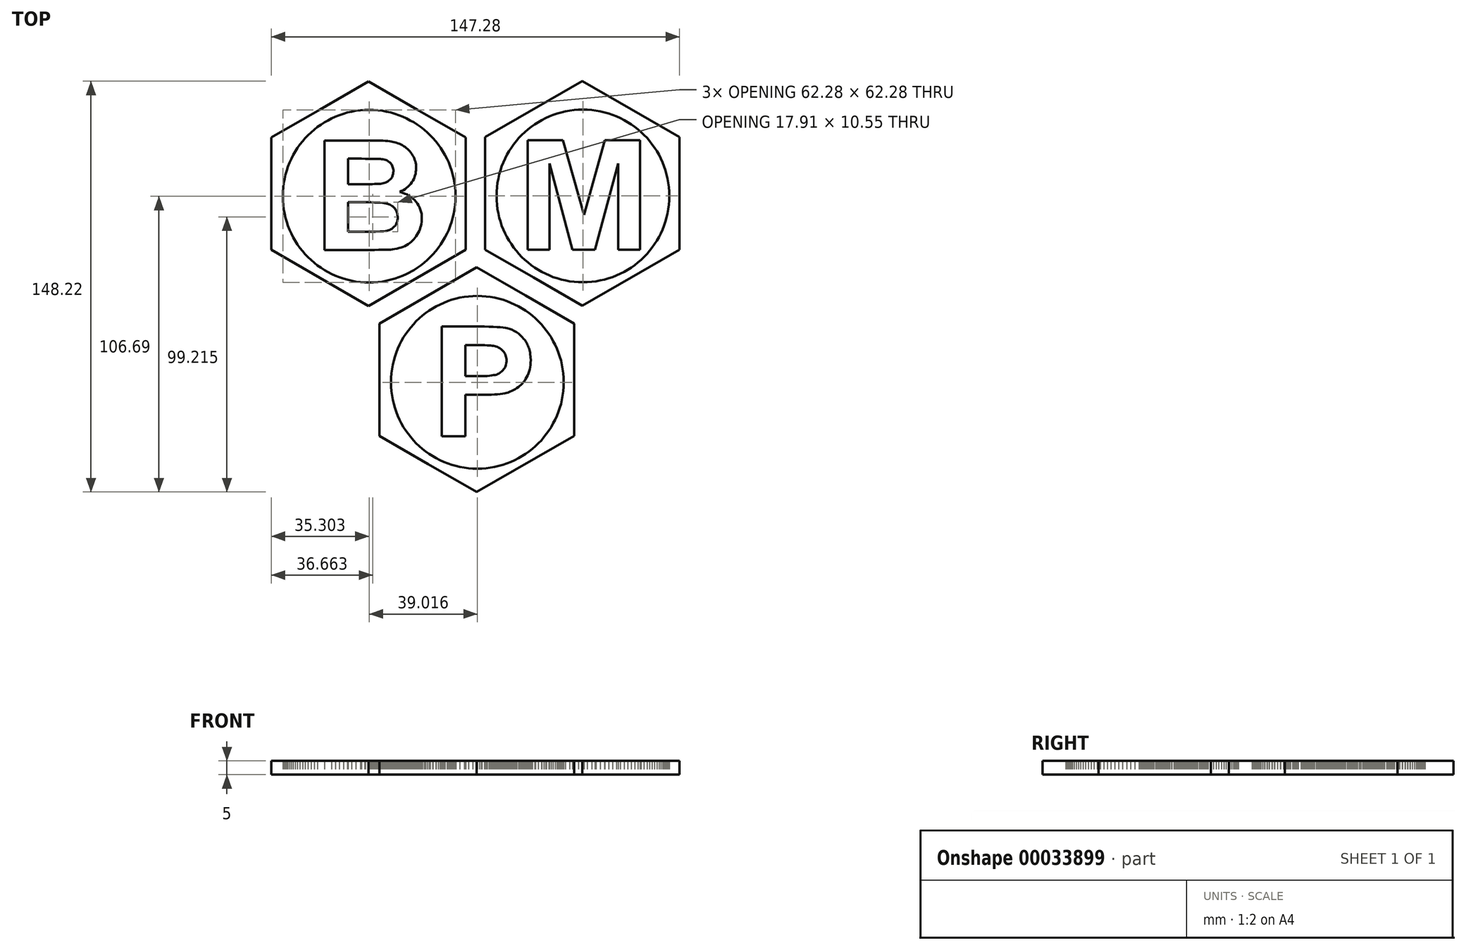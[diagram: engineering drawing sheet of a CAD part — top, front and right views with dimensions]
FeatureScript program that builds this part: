
annotation { "Feature Type Name" : "Feature", "Feature Type Description" : "" }
export const myFeature = defineFeature(function(context is Context, id is Id, definition is map)
    precondition{}
    {
        {
            var Q0;
            Q0=qCreatedBy(makeId("Top.planeOp"),FACE);
            var sketch = newSketch(context, id + "F0", { "sketchPlane" : qUnion([Q0])});
            skLineSegment(sketch, "E0", {"start": v(38.58, 74.11) * mm, "end": v(56.13, 64) * mm});
            skLineSegment(sketch, "E1", {"start": v(56.13, 64) * mm, "end": v(73.64, 53.89) * mm});
            skLineSegment(sketch, "E2", {"start": v(73.64, 53.89) * mm, "end": v(73.64, 33.62) * mm});
            skLineSegment(sketch, "E3", {"start": v(73.64, 33.62) * mm, "end": v(73.64, 13.35) * mm});
            skLineSegment(sketch, "E4", {"start": v(73.64, 13.35) * mm, "end": v(56.13, 3.24) * mm});
            skLineSegment(sketch, "E5", {"start": v(56.13, 3.24) * mm, "end": v(38.58, -6.92) * mm});
            skLineSegment(sketch, "E6", {"start": v(38.58, -6.92) * mm, "end": v(21.03, 3.24) * mm});
            skLineSegment(sketch, "E7", {"start": v(21.03, 3.24) * mm, "end": v(3.48, 13.35) * mm});
            skLineSegment(sketch, "E8", {"start": v(3.48, 13.35) * mm, "end": v(3.48, 33.62) * mm});
            skLineSegment(sketch, "E9", {"start": v(3.48, 33.62) * mm, "end": v(3.48, 53.89) * mm});
            skLineSegment(sketch, "E10", {"start": v(3.48, 53.89) * mm, "end": v(21.03, 64) * mm});
            skLineSegment(sketch, "E11", {"start": v(21.03, 64) * mm, "end": v(38.58, 74.11) * mm});
            skLineSegment(sketch, "E12", {"start": v(38.78, 63.84) * mm, "end": v(40.38, 63.8) * mm});
            skLineSegment(sketch, "E13", {"start": v(40.38, 63.8) * mm, "end": v(41.97, 63.68) * mm});
            skLineSegment(sketch, "E14", {"start": v(41.97, 63.68) * mm, "end": v(43.53, 63.48) * mm});
            skLineSegment(sketch, "E15", {"start": v(43.53, 63.48) * mm, "end": v(45.05, 63.2) * mm});
            skLineSegment(sketch, "E16", {"start": v(45.05, 63.2) * mm, "end": v(46.57, 62.84) * mm});
            skLineSegment(sketch, "E17", {"start": v(46.57, 62.84) * mm, "end": v(48.05, 62.44) * mm});
            skLineSegment(sketch, "E18", {"start": v(48.05, 62.44) * mm, "end": v(49.49, 61.96) * mm});
            skLineSegment(sketch, "E19", {"start": v(49.49, 61.96) * mm, "end": v(50.89, 61.4) * mm});
            skLineSegment(sketch, "E20", {"start": v(50.89, 61.4) * mm, "end": v(52.29, 60.76) * mm});
            skLineSegment(sketch, "E21", {"start": v(52.29, 60.76) * mm, "end": v(53.6, 60.08) * mm});
            skLineSegment(sketch, "E22", {"start": v(53.6, 60.08) * mm, "end": v(54.93, 59.32) * mm});
            skLineSegment(sketch, "E23", {"start": v(54.93, 59.32) * mm, "end": v(56.17, 58.52) * mm});
            skLineSegment(sketch, "E24", {"start": v(56.17, 58.52) * mm, "end": v(57.4, 57.64) * mm});
            skLineSegment(sketch, "E25", {"start": v(57.4, 57.64) * mm, "end": v(58.56, 56.73) * mm});
            skLineSegment(sketch, "E26", {"start": v(58.56, 56.73) * mm, "end": v(59.72, 55.77) * mm});
            skLineSegment(sketch, "E27", {"start": v(59.72, 55.77) * mm, "end": v(60.8, 54.73) * mm});
            skLineSegment(sketch, "E28", {"start": v(60.8, 54.73) * mm, "end": v(61.84, 53.65) * mm});
            skLineSegment(sketch, "E29", {"start": v(61.84, 53.65) * mm, "end": v(62.8, 52.49) * mm});
            skLineSegment(sketch, "E30", {"start": v(62.8, 52.49) * mm, "end": v(63.72, 51.33) * mm});
            skLineSegment(sketch, "E31", {"start": v(63.72, 51.33) * mm, "end": v(64.6, 50.09) * mm});
            skLineSegment(sketch, "E32", {"start": v(64.6, 50.09) * mm, "end": v(65.4, 48.85) * mm});
            skLineSegment(sketch, "E33", {"start": v(65.4, 48.85) * mm, "end": v(66.16, 47.53) * mm});
            skLineSegment(sketch, "E34", {"start": v(66.16, 47.53) * mm, "end": v(66.84, 46.21) * mm});
            skLineSegment(sketch, "E35", {"start": v(66.84, 46.21) * mm, "end": v(67.48, 44.81) * mm});
            skLineSegment(sketch, "E36", {"start": v(67.48, 44.81) * mm, "end": v(68.04, 43.41) * mm});
            skLineSegment(sketch, "E37", {"start": v(68.04, 43.41) * mm, "end": v(68.52, 41.97) * mm});
            skLineSegment(sketch, "E38", {"start": v(68.52, 41.97) * mm, "end": v(68.92, 40.5) * mm});
            skLineSegment(sketch, "E39", {"start": v(68.92, 40.5) * mm, "end": v(69.28, 38.98) * mm});
            skLineSegment(sketch, "E40", {"start": v(69.28, 38.98) * mm, "end": v(69.56, 37.46) * mm});
            skLineSegment(sketch, "E41", {"start": v(69.56, 37.46) * mm, "end": v(69.76, 35.9) * mm});
            skLineSegment(sketch, "E42", {"start": v(69.76, 35.9) * mm, "end": v(69.88, 34.3) * mm});
            skLineSegment(sketch, "E43", {"start": v(69.88, 34.3) * mm, "end": v(69.92, 32.7) * mm});
            skLineSegment(sketch, "E44", {"start": v(69.92, 32.7) * mm, "end": v(69.88, 31.1) * mm});
            skLineSegment(sketch, "E45", {"start": v(69.88, 31.1) * mm, "end": v(69.76, 29.5) * mm});
            skLineSegment(sketch, "E46", {"start": v(69.76, 29.5) * mm, "end": v(69.56, 27.94) * mm});
            skLineSegment(sketch, "E47", {"start": v(69.56, 27.94) * mm, "end": v(69.28, 26.42) * mm});
            skLineSegment(sketch, "E48", {"start": v(69.28, 26.42) * mm, "end": v(68.92, 24.9) * mm});
            skLineSegment(sketch, "E49", {"start": v(68.92, 24.9) * mm, "end": v(68.52, 23.43) * mm});
            skLineSegment(sketch, "E50", {"start": v(68.52, 23.43) * mm, "end": v(68.04, 21.99) * mm});
            skLineSegment(sketch, "E51", {"start": v(68.04, 21.99) * mm, "end": v(67.48, 20.59) * mm});
            skLineSegment(sketch, "E52", {"start": v(67.48, 20.59) * mm, "end": v(66.84, 19.19) * mm});
            skLineSegment(sketch, "E53", {"start": v(66.84, 19.19) * mm, "end": v(66.16, 17.87) * mm});
            skLineSegment(sketch, "E54", {"start": v(66.16, 17.87) * mm, "end": v(65.4, 16.55) * mm});
            skLineSegment(sketch, "E55", {"start": v(65.4, 16.55) * mm, "end": v(64.6, 15.27) * mm});
            skLineSegment(sketch, "E56", {"start": v(64.6, 15.27) * mm, "end": v(63.72, 14.07) * mm});
            skLineSegment(sketch, "E57", {"start": v(63.72, 14.07) * mm, "end": v(62.8, 12.87) * mm});
            skLineSegment(sketch, "E58", {"start": v(62.8, 12.87) * mm, "end": v(61.84, 11.75) * mm});
            skLineSegment(sketch, "E59", {"start": v(61.84, 11.75) * mm, "end": v(60.8, 10.67) * mm});
            skLineSegment(sketch, "E60", {"start": v(60.8, 10.67) * mm, "end": v(59.72, 9.63) * mm});
            skLineSegment(sketch, "E61", {"start": v(59.72, 9.63) * mm, "end": v(58.56, 8.67) * mm});
            skLineSegment(sketch, "E62", {"start": v(58.56, 8.67) * mm, "end": v(57.4, 7.76) * mm});
            skLineSegment(sketch, "E63", {"start": v(57.4, 7.76) * mm, "end": v(56.17, 6.88) * mm});
            skLineSegment(sketch, "E64", {"start": v(56.17, 6.88) * mm, "end": v(54.93, 6.08) * mm});
            skLineSegment(sketch, "E65", {"start": v(54.93, 6.08) * mm, "end": v(53.6, 5.32) * mm});
            skLineSegment(sketch, "E66", {"start": v(53.6, 5.32) * mm, "end": v(52.29, 4.64) * mm});
            skLineSegment(sketch, "E67", {"start": v(52.29, 4.64) * mm, "end": v(50.89, 4) * mm});
            skLineSegment(sketch, "E68", {"start": v(50.89, 4) * mm, "end": v(49.49, 3.44) * mm});
            skLineSegment(sketch, "E69", {"start": v(49.49, 3.44) * mm, "end": v(48.05, 2.96) * mm});
            skLineSegment(sketch, "E70", {"start": v(48.05, 2.96) * mm, "end": v(46.57, 2.52) * mm});
            skLineSegment(sketch, "E71", {"start": v(46.57, 2.52) * mm, "end": v(45.05, 2.2) * mm});
            skLineSegment(sketch, "E72", {"start": v(45.05, 2.2) * mm, "end": v(43.53, 1.92) * mm});
            skLineSegment(sketch, "E73", {"start": v(43.53, 1.92) * mm, "end": v(41.97, 1.72) * mm});
            skLineSegment(sketch, "E74", {"start": v(41.97, 1.72) * mm, "end": v(40.38, 1.6) * mm});
            skLineSegment(sketch, "E75", {"start": v(40.38, 1.6) * mm, "end": v(38.78, 1.56) * mm});
            skLineSegment(sketch, "E76", {"start": v(38.78, 1.56) * mm, "end": v(37.18, 1.6) * mm});
            skLineSegment(sketch, "E77", {"start": v(37.18, 1.6) * mm, "end": v(35.58, 1.72) * mm});
            skLineSegment(sketch, "E78", {"start": v(35.58, 1.72) * mm, "end": v(34.02, 1.92) * mm});
            skLineSegment(sketch, "E79", {"start": v(34.02, 1.92) * mm, "end": v(32.5, 2.2) * mm});
            skLineSegment(sketch, "E80", {"start": v(32.5, 2.2) * mm, "end": v(30.98, 2.52) * mm});
            skLineSegment(sketch, "E81", {"start": v(30.98, 2.52) * mm, "end": v(29.5, 2.96) * mm});
            skLineSegment(sketch, "E82", {"start": v(29.5, 2.96) * mm, "end": v(28.06, 3.44) * mm});
            skLineSegment(sketch, "E83", {"start": v(28.06, 3.44) * mm, "end": v(26.66, 4) * mm});
            skLineSegment(sketch, "E84", {"start": v(26.66, 4) * mm, "end": v(25.26, 4.64) * mm});
            skLineSegment(sketch, "E85", {"start": v(25.26, 4.64) * mm, "end": v(23.95, 5.32) * mm});
            skLineSegment(sketch, "E86", {"start": v(23.95, 5.32) * mm, "end": v(22.63, 6.08) * mm});
            skLineSegment(sketch, "E87", {"start": v(22.63, 6.08) * mm, "end": v(21.35, 6.88) * mm});
            skLineSegment(sketch, "E88", {"start": v(21.35, 6.88) * mm, "end": v(20.15, 7.76) * mm});
            skLineSegment(sketch, "E89", {"start": v(20.15, 7.76) * mm, "end": v(18.95, 8.67) * mm});
            skLineSegment(sketch, "E90", {"start": v(18.95, 8.67) * mm, "end": v(17.83, 9.63) * mm});
            skLineSegment(sketch, "E91", {"start": v(17.83, 9.63) * mm, "end": v(16.75, 10.67) * mm});
            skLineSegment(sketch, "E92", {"start": v(16.75, 10.67) * mm, "end": v(15.71, 11.75) * mm});
            skLineSegment(sketch, "E93", {"start": v(15.71, 11.75) * mm, "end": v(14.75, 12.87) * mm});
            skLineSegment(sketch, "E94", {"start": v(14.75, 12.87) * mm, "end": v(13.83, 14.07) * mm});
            skLineSegment(sketch, "E95", {"start": v(13.83, 14.07) * mm, "end": v(12.95, 15.27) * mm});
            skLineSegment(sketch, "E96", {"start": v(12.95, 15.27) * mm, "end": v(12.15, 16.55) * mm});
            skLineSegment(sketch, "E97", {"start": v(12.15, 16.55) * mm, "end": v(11.4, 17.87) * mm});
            skLineSegment(sketch, "E98", {"start": v(11.4, 17.87) * mm, "end": v(10.71, 19.19) * mm});
            skLineSegment(sketch, "E99", {"start": v(10.71, 19.19) * mm, "end": v(10.07, 20.59) * mm});
            skLineSegment(sketch, "E100", {"start": v(10.07, 20.59) * mm, "end": v(9.51, 21.99) * mm});
            skLineSegment(sketch, "E101", {"start": v(9.51, 21.99) * mm, "end": v(9.03, 23.43) * mm});
            skLineSegment(sketch, "E102", {"start": v(9.03, 23.43) * mm, "end": v(8.6, 24.9) * mm});
            skLineSegment(sketch, "E103", {"start": v(8.6, 24.9) * mm, "end": v(8.27, 26.42) * mm});
            skLineSegment(sketch, "E104", {"start": v(8.27, 26.42) * mm, "end": v(8, 27.94) * mm});
            skLineSegment(sketch, "E105", {"start": v(8, 27.94) * mm, "end": v(7.8, 29.5) * mm});
            skLineSegment(sketch, "E106", {"start": v(7.8, 29.5) * mm, "end": v(7.68, 31.1) * mm});
            skLineSegment(sketch, "E107", {"start": v(7.68, 31.1) * mm, "end": v(7.64, 32.7) * mm});
            skLineSegment(sketch, "E108", {"start": v(7.64, 32.7) * mm, "end": v(7.68, 34.3) * mm});
            skLineSegment(sketch, "E109", {"start": v(7.68, 34.3) * mm, "end": v(7.8, 35.9) * mm});
            skLineSegment(sketch, "E110", {"start": v(7.8, 35.9) * mm, "end": v(8, 37.46) * mm});
            skLineSegment(sketch, "E111", {"start": v(8, 37.46) * mm, "end": v(8.27, 38.98) * mm});
            skLineSegment(sketch, "E112", {"start": v(8.27, 38.98) * mm, "end": v(8.6, 40.5) * mm});
            skLineSegment(sketch, "E113", {"start": v(8.6, 40.5) * mm, "end": v(9.03, 41.97) * mm});
            skLineSegment(sketch, "E114", {"start": v(9.03, 41.97) * mm, "end": v(9.51, 43.41) * mm});
            skLineSegment(sketch, "E115", {"start": v(9.51, 43.41) * mm, "end": v(10.07, 44.81) * mm});
            skLineSegment(sketch, "E116", {"start": v(10.07, 44.81) * mm, "end": v(10.71, 46.21) * mm});
            skLineSegment(sketch, "E117", {"start": v(10.71, 46.21) * mm, "end": v(11.4, 47.53) * mm});
            skLineSegment(sketch, "E118", {"start": v(11.4, 47.53) * mm, "end": v(12.15, 48.85) * mm});
            skLineSegment(sketch, "E119", {"start": v(12.15, 48.85) * mm, "end": v(12.95, 50.09) * mm});
            skLineSegment(sketch, "E120", {"start": v(12.95, 50.09) * mm, "end": v(13.83, 51.33) * mm});
            skLineSegment(sketch, "E121", {"start": v(13.83, 51.33) * mm, "end": v(14.75, 52.49) * mm});
            skLineSegment(sketch, "E122", {"start": v(14.75, 52.49) * mm, "end": v(15.71, 53.65) * mm});
            skLineSegment(sketch, "E123", {"start": v(15.71, 53.65) * mm, "end": v(16.75, 54.73) * mm});
            skLineSegment(sketch, "E124", {"start": v(16.75, 54.73) * mm, "end": v(17.83, 55.77) * mm});
            skLineSegment(sketch, "E125", {"start": v(17.83, 55.77) * mm, "end": v(18.95, 56.73) * mm});
            skLineSegment(sketch, "E126", {"start": v(18.95, 56.73) * mm, "end": v(20.15, 57.64) * mm});
            skLineSegment(sketch, "E127", {"start": v(20.15, 57.64) * mm, "end": v(21.35, 58.52) * mm});
            skLineSegment(sketch, "E128", {"start": v(21.35, 58.52) * mm, "end": v(22.63, 59.32) * mm});
            skLineSegment(sketch, "E129", {"start": v(22.63, 59.32) * mm, "end": v(23.95, 60.08) * mm});
            skLineSegment(sketch, "E130", {"start": v(23.95, 60.08) * mm, "end": v(25.26, 60.76) * mm});
            skLineSegment(sketch, "E131", {"start": v(25.26, 60.76) * mm, "end": v(26.66, 61.4) * mm});
            skLineSegment(sketch, "E132", {"start": v(26.66, 61.4) * mm, "end": v(28.06, 61.96) * mm});
            skLineSegment(sketch, "E133", {"start": v(28.06, 61.96) * mm, "end": v(29.5, 62.44) * mm});
            skLineSegment(sketch, "E134", {"start": v(29.5, 62.44) * mm, "end": v(30.98, 62.84) * mm});
            skLineSegment(sketch, "E135", {"start": v(30.98, 62.84) * mm, "end": v(32.5, 63.2) * mm});
            skLineSegment(sketch, "E136", {"start": v(32.5, 63.2) * mm, "end": v(34.02, 63.48) * mm});
            skLineSegment(sketch, "E137", {"start": v(34.02, 63.48) * mm, "end": v(35.58, 63.68) * mm});
            skLineSegment(sketch, "E138", {"start": v(35.58, 63.68) * mm, "end": v(37.18, 63.8) * mm});
            skLineSegment(sketch, "E139", {"start": v(37.18, 63.8) * mm, "end": v(38.78, 63.84) * mm});
            skLineSegment(sketch, "E140", {"start": v(18.87, 13.23) * mm, "end": v(18.87, 52.8) * mm});
            skLineSegment(sketch, "E141", {"start": v(18.87, 52.8) * mm, "end": v(31.54, 52.8) * mm});
            skLineSegment(sketch, "E142", {"start": v(31.54, 52.8) * mm, "end": v(39.14, 25.82) * mm});
            skLineSegment(sketch, "E143", {"start": v(39.14, 25.82) * mm, "end": v(46.61, 52.8) * mm});
            skLineSegment(sketch, "E144", {"start": v(46.61, 52.8) * mm, "end": v(59.32, 52.8) * mm});
            skLineSegment(sketch, "E145", {"start": v(59.32, 52.8) * mm, "end": v(59.32, 13.23) * mm});
            skLineSegment(sketch, "E146", {"start": v(59.32, 13.23) * mm, "end": v(51.45, 13.23) * mm});
            skLineSegment(sketch, "E147", {"start": v(51.45, 13.23) * mm, "end": v(51.45, 44.37) * mm});
            skLineSegment(sketch, "E148", {"start": v(51.45, 44.37) * mm, "end": v(43.13, 13.23) * mm});
            skLineSegment(sketch, "E149", {"start": v(43.13, 13.23) * mm, "end": v(35.02, 13.23) * mm});
            skLineSegment(sketch, "E150", {"start": v(35.02, 13.23) * mm, "end": v(26.7, 44.37) * mm});
            skLineSegment(sketch, "E151", {"start": v(26.7, 44.37) * mm, "end": v(26.7, 13.23) * mm});
            skLineSegment(sketch, "E152", {"start": v(26.7, 13.23) * mm, "end": v(18.87, 13.23) * mm});
            skLineSegment(sketch, "E153", {"start": v(-38.54, 74.03) * mm, "end": v(-20.99, 63.88) * mm});
            skLineSegment(sketch, "E154", {"start": v(-20.99, 63.88) * mm, "end": v(-3.44, 53.77) * mm});
            skLineSegment(sketch, "E155", {"start": v(-3.44, 53.77) * mm, "end": v(-3.44, 33.5) * mm});
            skLineSegment(sketch, "E156", {"start": v(-3.44, 33.5) * mm, "end": v(-3.44, 13.27) * mm});
            skLineSegment(sketch, "E157", {"start": v(-3.44, 13.27) * mm, "end": v(-20.99, 3.12) * mm});
            skLineSegment(sketch, "E158", {"start": v(-20.99, 3.12) * mm, "end": v(-38.54, -7) * mm});
            skLineSegment(sketch, "E159", {"start": v(-38.54, -7) * mm, "end": v(-56.09, 3.12) * mm});
            skLineSegment(sketch, "E160", {"start": v(-56.09, 3.12) * mm, "end": v(-73.64, 13.27) * mm});
            skLineSegment(sketch, "E161", {"start": v(-73.64, 13.27) * mm, "end": v(-73.64, 33.5) * mm});
            skLineSegment(sketch, "E162", {"start": v(-73.64, 33.5) * mm, "end": v(-73.64, 53.77) * mm});
            skLineSegment(sketch, "E163", {"start": v(-73.64, 53.77) * mm, "end": v(-56.09, 63.88) * mm});
            skLineSegment(sketch, "E164", {"start": v(-56.09, 63.88) * mm, "end": v(-38.54, 74.03) * mm});
            skLineSegment(sketch, "E165", {"start": v(-38.34, 63.72) * mm, "end": v(-36.74, 63.68) * mm});
            skLineSegment(sketch, "E166", {"start": v(-36.74, 63.68) * mm, "end": v(-35.14, 63.56) * mm});
            skLineSegment(sketch, "E167", {"start": v(-35.14, 63.56) * mm, "end": v(-33.58, 63.4) * mm});
            skLineSegment(sketch, "E168", {"start": v(-33.58, 63.4) * mm, "end": v(-32.06, 63.12) * mm});
            skLineSegment(sketch, "E169", {"start": v(-32.06, 63.12) * mm, "end": v(-30.54, 62.76) * mm});
            skLineSegment(sketch, "E170", {"start": v(-30.54, 62.76) * mm, "end": v(-29.06, 62.32) * mm});
            skLineSegment(sketch, "E171", {"start": v(-29.06, 62.32) * mm, "end": v(-27.62, 61.84) * mm});
            skLineSegment(sketch, "E172", {"start": v(-27.62, 61.84) * mm, "end": v(-26.22, 61.28) * mm});
            skLineSegment(sketch, "E173", {"start": v(-26.22, 61.28) * mm, "end": v(-24.82, 60.68) * mm});
            skLineSegment(sketch, "E174", {"start": v(-24.82, 60.68) * mm, "end": v(-23.5, 59.96) * mm});
            skLineSegment(sketch, "E175", {"start": v(-23.5, 59.96) * mm, "end": v(-22.19, 59.24) * mm});
            skLineSegment(sketch, "E176", {"start": v(-22.19, 59.24) * mm, "end": v(-20.9, 58.4) * mm});
            skLineSegment(sketch, "E177", {"start": v(-20.9, 58.4) * mm, "end": v(-19.7, 57.56) * mm});
            skLineSegment(sketch, "E178", {"start": v(-19.7, 57.56) * mm, "end": v(-18.5, 56.65) * mm});
            skLineSegment(sketch, "E179", {"start": v(-18.5, 56.65) * mm, "end": v(-17.39, 55.65) * mm});
            skLineSegment(sketch, "E180", {"start": v(-17.39, 55.65) * mm, "end": v(-16.31, 54.6) * mm});
            skLineSegment(sketch, "E181", {"start": v(-16.31, 54.6) * mm, "end": v(-15.27, 53.53) * mm});
            skLineSegment(sketch, "E182", {"start": v(-15.27, 53.53) * mm, "end": v(-14.31, 52.4) * mm});
            skLineSegment(sketch, "E183", {"start": v(-14.31, 52.4) * mm, "end": v(-13.4, 51.25) * mm});
            skLineSegment(sketch, "E184", {"start": v(-13.4, 51.25) * mm, "end": v(-12.51, 50) * mm});
            skLineSegment(sketch, "E185", {"start": v(-12.51, 50) * mm, "end": v(-11.71, 48.73) * mm});
            skLineSegment(sketch, "E186", {"start": v(-11.71, 48.73) * mm, "end": v(-10.95, 47.45) * mm});
            skLineSegment(sketch, "E187", {"start": v(-10.95, 47.45) * mm, "end": v(-10.27, 46.1) * mm});
            skLineSegment(sketch, "E188", {"start": v(-10.27, 46.1) * mm, "end": v(-9.63, 44.73) * mm});
            skLineSegment(sketch, "E189", {"start": v(-9.63, 44.73) * mm, "end": v(-9.07, 43.3) * mm});
            skLineSegment(sketch, "E190", {"start": v(-9.07, 43.3) * mm, "end": v(-8.6, 41.85) * mm});
            skLineSegment(sketch, "E191", {"start": v(-8.6, 41.85) * mm, "end": v(-8.16, 40.38) * mm});
            skLineSegment(sketch, "E192", {"start": v(-8.16, 40.38) * mm, "end": v(-7.84, 38.86) * mm});
            skLineSegment(sketch, "E193", {"start": v(-7.84, 38.86) * mm, "end": v(-7.56, 37.34) * mm});
            skLineSegment(sketch, "E194", {"start": v(-7.56, 37.34) * mm, "end": v(-7.36, 35.78) * mm});
            skLineSegment(sketch, "E195", {"start": v(-7.36, 35.78) * mm, "end": v(-7.24, 34.22) * mm});
            skLineSegment(sketch, "E196", {"start": v(-7.24, 34.22) * mm, "end": v(-7.2, 32.58) * mm});
            skLineSegment(sketch, "E197", {"start": v(-7.2, 32.58) * mm, "end": v(-7.24, 30.98) * mm});
            skLineSegment(sketch, "E198", {"start": v(-7.24, 30.98) * mm, "end": v(-7.36, 29.42) * mm});
            skLineSegment(sketch, "E199", {"start": v(-7.36, 29.42) * mm, "end": v(-7.56, 27.86) * mm});
            skLineSegment(sketch, "E200", {"start": v(-7.56, 27.86) * mm, "end": v(-7.84, 26.3) * mm});
            skLineSegment(sketch, "E201", {"start": v(-7.84, 26.3) * mm, "end": v(-8.16, 24.82) * mm});
            skLineSegment(sketch, "E202", {"start": v(-8.16, 24.82) * mm, "end": v(-8.6, 23.35) * mm});
            skLineSegment(sketch, "E203", {"start": v(-8.6, 23.35) * mm, "end": v(-9.07, 21.9) * mm});
            skLineSegment(sketch, "E204", {"start": v(-9.07, 21.9) * mm, "end": v(-9.63, 20.47) * mm});
            skLineSegment(sketch, "E205", {"start": v(-9.63, 20.47) * mm, "end": v(-10.27, 19.1) * mm});
            skLineSegment(sketch, "E206", {"start": v(-10.27, 19.1) * mm, "end": v(-10.95, 17.75) * mm});
            skLineSegment(sketch, "E207", {"start": v(-10.95, 17.75) * mm, "end": v(-11.71, 16.47) * mm});
            skLineSegment(sketch, "E208", {"start": v(-11.71, 16.47) * mm, "end": v(-12.51, 15.2) * mm});
            skLineSegment(sketch, "E209", {"start": v(-12.51, 15.2) * mm, "end": v(-13.4, 13.95) * mm});
            skLineSegment(sketch, "E210", {"start": v(-13.4, 13.95) * mm, "end": v(-14.31, 12.8) * mm});
            skLineSegment(sketch, "E211", {"start": v(-14.31, 12.8) * mm, "end": v(-15.27, 11.67) * mm});
            skLineSegment(sketch, "E212", {"start": v(-15.27, 11.67) * mm, "end": v(-16.31, 10.6) * mm});
            skLineSegment(sketch, "E213", {"start": v(-16.31, 10.6) * mm, "end": v(-17.39, 9.55) * mm});
            skLineSegment(sketch, "E214", {"start": v(-17.39, 9.55) * mm, "end": v(-18.5, 8.55) * mm});
            skLineSegment(sketch, "E215", {"start": v(-18.5, 8.55) * mm, "end": v(-19.7, 7.64) * mm});
            skLineSegment(sketch, "E216", {"start": v(-19.7, 7.64) * mm, "end": v(-20.9, 6.8) * mm});
            skLineSegment(sketch, "E217", {"start": v(-20.9, 6.8) * mm, "end": v(-22.19, 5.96) * mm});
            skLineSegment(sketch, "E218", {"start": v(-22.19, 5.96) * mm, "end": v(-23.5, 5.24) * mm});
            skLineSegment(sketch, "E219", {"start": v(-23.5, 5.24) * mm, "end": v(-24.82, 4.52) * mm});
            skLineSegment(sketch, "E220", {"start": v(-24.82, 4.52) * mm, "end": v(-26.22, 3.92) * mm});
            skLineSegment(sketch, "E221", {"start": v(-26.22, 3.92) * mm, "end": v(-27.62, 3.36) * mm});
            skLineSegment(sketch, "E222", {"start": v(-27.62, 3.36) * mm, "end": v(-29.06, 2.84) * mm});
            skLineSegment(sketch, "E223", {"start": v(-29.06, 2.84) * mm, "end": v(-30.54, 2.44) * mm});
            skLineSegment(sketch, "E224", {"start": v(-30.54, 2.44) * mm, "end": v(-32.06, 2.08) * mm});
            skLineSegment(sketch, "E225", {"start": v(-32.06, 2.08) * mm, "end": v(-33.58, 1.8) * mm});
            skLineSegment(sketch, "E226", {"start": v(-33.58, 1.8) * mm, "end": v(-35.14, 1.6) * mm});
            skLineSegment(sketch, "E227", {"start": v(-35.14, 1.6) * mm, "end": v(-36.74, 1.48) * mm});
            skLineSegment(sketch, "E228", {"start": v(-36.74, 1.48) * mm, "end": v(-38.34, 1.44) * mm});
            skLineSegment(sketch, "E229", {"start": v(-38.34, 1.44) * mm, "end": v(-39.94, 1.48) * mm});
            skLineSegment(sketch, "E230", {"start": v(-39.94, 1.48) * mm, "end": v(-41.53, 1.6) * mm});
            skLineSegment(sketch, "E231", {"start": v(-41.53, 1.6) * mm, "end": v(-43.1, 1.8) * mm});
            skLineSegment(sketch, "E232", {"start": v(-43.1, 1.8) * mm, "end": v(-44.61, 2.08) * mm});
            skLineSegment(sketch, "E233", {"start": v(-44.61, 2.08) * mm, "end": v(-46.13, 2.44) * mm});
            skLineSegment(sketch, "E234", {"start": v(-46.13, 2.44) * mm, "end": v(-47.61, 2.84) * mm});
            skLineSegment(sketch, "E235", {"start": v(-47.61, 2.84) * mm, "end": v(-49.05, 3.36) * mm});
            skLineSegment(sketch, "E236", {"start": v(-49.05, 3.36) * mm, "end": v(-50.45, 3.92) * mm});
            skLineSegment(sketch, "E237", {"start": v(-50.45, 3.92) * mm, "end": v(-51.85, 4.52) * mm});
            skLineSegment(sketch, "E238", {"start": v(-51.85, 4.52) * mm, "end": v(-53.17, 5.24) * mm});
            skLineSegment(sketch, "E239", {"start": v(-53.17, 5.24) * mm, "end": v(-54.49, 5.96) * mm});
            skLineSegment(sketch, "E240", {"start": v(-54.49, 5.96) * mm, "end": v(-55.73, 6.8) * mm});
            skLineSegment(sketch, "E241", {"start": v(-55.73, 6.8) * mm, "end": v(-56.97, 7.64) * mm});
            skLineSegment(sketch, "E242", {"start": v(-56.97, 7.64) * mm, "end": v(-58.12, 8.55) * mm});
            skLineSegment(sketch, "E243", {"start": v(-58.12, 8.55) * mm, "end": v(-59.28, 9.55) * mm});
            skLineSegment(sketch, "E244", {"start": v(-59.28, 9.55) * mm, "end": v(-60.36, 10.6) * mm});
            skLineSegment(sketch, "E245", {"start": v(-60.36, 10.6) * mm, "end": v(-61.4, 11.67) * mm});
            skLineSegment(sketch, "E246", {"start": v(-61.4, 11.67) * mm, "end": v(-62.36, 12.8) * mm});
            skLineSegment(sketch, "E247", {"start": v(-62.36, 12.8) * mm, "end": v(-63.28, 13.95) * mm});
            skLineSegment(sketch, "E248", {"start": v(-63.28, 13.95) * mm, "end": v(-64.16, 15.2) * mm});
            skLineSegment(sketch, "E249", {"start": v(-64.16, 15.2) * mm, "end": v(-64.96, 16.47) * mm});
            skLineSegment(sketch, "E250", {"start": v(-64.96, 16.47) * mm, "end": v(-65.72, 17.75) * mm});
            skLineSegment(sketch, "E251", {"start": v(-65.72, 17.75) * mm, "end": v(-66.4, 19.1) * mm});
            skLineSegment(sketch, "E252", {"start": v(-66.4, 19.1) * mm, "end": v(-67.04, 20.47) * mm});
            skLineSegment(sketch, "E253", {"start": v(-67.04, 20.47) * mm, "end": v(-67.6, 21.9) * mm});
            skLineSegment(sketch, "E254", {"start": v(-67.6, 21.9) * mm, "end": v(-68.08, 23.35) * mm});
            skLineSegment(sketch, "E255", {"start": v(-68.08, 23.35) * mm, "end": v(-68.48, 24.82) * mm});
            skLineSegment(sketch, "E256", {"start": v(-68.48, 24.82) * mm, "end": v(-68.84, 26.3) * mm});
            skLineSegment(sketch, "E257", {"start": v(-68.84, 26.3) * mm, "end": v(-69.12, 27.86) * mm});
            skLineSegment(sketch, "E258", {"start": v(-69.12, 27.86) * mm, "end": v(-69.32, 29.42) * mm});
            skLineSegment(sketch, "E259", {"start": v(-69.32, 29.42) * mm, "end": v(-69.44, 30.98) * mm});
            skLineSegment(sketch, "E260", {"start": v(-69.44, 30.98) * mm, "end": v(-69.48, 32.58) * mm});
            skLineSegment(sketch, "E261", {"start": v(-69.48, 32.58) * mm, "end": v(-69.44, 34.22) * mm});
            skLineSegment(sketch, "E262", {"start": v(-69.44, 34.22) * mm, "end": v(-69.32, 35.78) * mm});
            skLineSegment(sketch, "E263", {"start": v(-69.32, 35.78) * mm, "end": v(-69.12, 37.34) * mm});
            skLineSegment(sketch, "E264", {"start": v(-69.12, 37.34) * mm, "end": v(-68.84, 38.86) * mm});
            skLineSegment(sketch, "E265", {"start": v(-68.84, 38.86) * mm, "end": v(-68.48, 40.38) * mm});
            skLineSegment(sketch, "E266", {"start": v(-68.48, 40.38) * mm, "end": v(-68.08, 41.85) * mm});
            skLineSegment(sketch, "E267", {"start": v(-68.08, 41.85) * mm, "end": v(-67.6, 43.3) * mm});
            skLineSegment(sketch, "E268", {"start": v(-67.6, 43.3) * mm, "end": v(-67.04, 44.73) * mm});
            skLineSegment(sketch, "E269", {"start": v(-67.04, 44.73) * mm, "end": v(-66.4, 46.1) * mm});
            skLineSegment(sketch, "E270", {"start": v(-66.4, 46.1) * mm, "end": v(-65.72, 47.45) * mm});
            skLineSegment(sketch, "E271", {"start": v(-65.72, 47.45) * mm, "end": v(-64.96, 48.73) * mm});
            skLineSegment(sketch, "E272", {"start": v(-64.96, 48.73) * mm, "end": v(-64.16, 50) * mm});
            skLineSegment(sketch, "E273", {"start": v(-64.16, 50) * mm, "end": v(-63.28, 51.25) * mm});
            skLineSegment(sketch, "E274", {"start": v(-63.28, 51.25) * mm, "end": v(-62.36, 52.4) * mm});
            skLineSegment(sketch, "E275", {"start": v(-62.36, 52.4) * mm, "end": v(-61.4, 53.53) * mm});
            skLineSegment(sketch, "E276", {"start": v(-61.4, 53.53) * mm, "end": v(-60.36, 54.6) * mm});
            skLineSegment(sketch, "E277", {"start": v(-60.36, 54.6) * mm, "end": v(-59.28, 55.65) * mm});
            skLineSegment(sketch, "E278", {"start": v(-59.28, 55.65) * mm, "end": v(-58.12, 56.65) * mm});
            skLineSegment(sketch, "E279", {"start": v(-58.12, 56.65) * mm, "end": v(-56.97, 57.56) * mm});
            skLineSegment(sketch, "E280", {"start": v(-56.97, 57.56) * mm, "end": v(-55.73, 58.4) * mm});
            skLineSegment(sketch, "E281", {"start": v(-55.73, 58.4) * mm, "end": v(-54.49, 59.24) * mm});
            skLineSegment(sketch, "E282", {"start": v(-54.49, 59.24) * mm, "end": v(-53.17, 59.96) * mm});
            skLineSegment(sketch, "E283", {"start": v(-53.17, 59.96) * mm, "end": v(-51.85, 60.68) * mm});
            skLineSegment(sketch, "E284", {"start": v(-51.85, 60.68) * mm, "end": v(-50.45, 61.28) * mm});
            skLineSegment(sketch, "E285", {"start": v(-50.45, 61.28) * mm, "end": v(-49.05, 61.84) * mm});
            skLineSegment(sketch, "E286", {"start": v(-49.05, 61.84) * mm, "end": v(-47.61, 62.32) * mm});
            skLineSegment(sketch, "E287", {"start": v(-47.61, 62.32) * mm, "end": v(-46.13, 62.76) * mm});
            skLineSegment(sketch, "E288", {"start": v(-46.13, 62.76) * mm, "end": v(-44.61, 63.12) * mm});
            skLineSegment(sketch, "E289", {"start": v(-44.61, 63.12) * mm, "end": v(-43.1, 63.4) * mm});
            skLineSegment(sketch, "E290", {"start": v(-43.1, 63.4) * mm, "end": v(-41.53, 63.56) * mm});
            skLineSegment(sketch, "E291", {"start": v(-41.53, 63.56) * mm, "end": v(-39.94, 63.68) * mm});
            skLineSegment(sketch, "E292", {"start": v(-39.94, 63.68) * mm, "end": v(-38.34, 63.72) * mm});
            skLineSegment(sketch, "E293", {"start": v(-54.37, 52.69) * mm, "end": v(-37.66, 52.69) * mm});
            skLineSegment(sketch, "E294", {"start": v(-37.66, 52.69) * mm, "end": v(-36.42, 52.69) * mm});
            skLineSegment(sketch, "E295", {"start": v(-36.42, 52.69) * mm, "end": v(-35.3, 52.69) * mm});
            skLineSegment(sketch, "E296", {"start": v(-35.3, 52.69) * mm, "end": v(-34.26, 52.65) * mm});
            skLineSegment(sketch, "E297", {"start": v(-34.26, 52.65) * mm, "end": v(-33.3, 52.6) * mm});
            skLineSegment(sketch, "E298", {"start": v(-33.3, 52.6) * mm, "end": v(-32.42, 52.53) * mm});
            skLineSegment(sketch, "E299", {"start": v(-32.42, 52.53) * mm, "end": v(-31.58, 52.49) * mm});
            skLineSegment(sketch, "E300", {"start": v(-31.58, 52.49) * mm, "end": v(-30.86, 52.4) * mm});
            skLineSegment(sketch, "E301", {"start": v(-30.86, 52.4) * mm, "end": v(-30.22, 52.29) * mm});
            skLineSegment(sketch, "E302", {"start": v(-30.22, 52.29) * mm, "end": v(-29.62, 52.2) * mm});
            skLineSegment(sketch, "E303", {"start": v(-29.62, 52.2) * mm, "end": v(-29.02, 52.05) * mm});
            skLineSegment(sketch, "E304", {"start": v(-29.02, 52.05) * mm, "end": v(-28.46, 51.89) * mm});
            skLineSegment(sketch, "E305", {"start": v(-28.46, 51.89) * mm, "end": v(-27.9, 51.69) * mm});
            skLineSegment(sketch, "E306", {"start": v(-27.9, 51.69) * mm, "end": v(-27.38, 51.49) * mm});
            skLineSegment(sketch, "E307", {"start": v(-27.38, 51.49) * mm, "end": v(-26.86, 51.25) * mm});
            skLineSegment(sketch, "E308", {"start": v(-26.86, 51.25) * mm, "end": v(-26.34, 50.97) * mm});
            skLineSegment(sketch, "E309", {"start": v(-26.34, 50.97) * mm, "end": v(-25.86, 50.69) * mm});
            skLineSegment(sketch, "E310", {"start": v(-25.86, 50.69) * mm, "end": v(-25.38, 50.33) * mm});
            skLineSegment(sketch, "E311", {"start": v(-25.38, 50.33) * mm, "end": v(-24.94, 50) * mm});
            skLineSegment(sketch, "E312", {"start": v(-24.94, 50) * mm, "end": v(-24.5, 49.6) * mm});
            skLineSegment(sketch, "E313", {"start": v(-24.5, 49.6) * mm, "end": v(-24.07, 49.21) * mm});
            skLineSegment(sketch, "E314", {"start": v(-24.07, 49.21) * mm, "end": v(-23.7, 48.81) * mm});
            skLineSegment(sketch, "E315", {"start": v(-23.7, 48.81) * mm, "end": v(-23.3, 48.33) * mm});
            skLineSegment(sketch, "E316", {"start": v(-23.3, 48.33) * mm, "end": v(-22.99, 47.85) * mm});
            skLineSegment(sketch, "E317", {"start": v(-22.99, 47.85) * mm, "end": v(-22.63, 47.37) * mm});
            skLineSegment(sketch, "E318", {"start": v(-22.63, 47.37) * mm, "end": v(-22.35, 46.85) * mm});
            skLineSegment(sketch, "E319", {"start": v(-22.35, 46.85) * mm, "end": v(-22.07, 46.3) * mm});
            skLineSegment(sketch, "E320", {"start": v(-22.07, 46.3) * mm, "end": v(-21.87, 45.73) * mm});
            skLineSegment(sketch, "E321", {"start": v(-21.87, 45.73) * mm, "end": v(-21.67, 45.17) * mm});
            skLineSegment(sketch, "E322", {"start": v(-21.67, 45.17) * mm, "end": v(-21.55, 44.61) * mm});
            skLineSegment(sketch, "E323", {"start": v(-21.55, 44.61) * mm, "end": v(-21.43, 43.97) * mm});
            skLineSegment(sketch, "E324", {"start": v(-21.43, 43.97) * mm, "end": v(-21.39, 43.37) * mm});
            skLineSegment(sketch, "E325", {"start": v(-21.39, 43.37) * mm, "end": v(-21.35, 42.73) * mm});
            skLineSegment(sketch, "E326", {"start": v(-21.35, 42.73) * mm, "end": v(-21.39, 42.05) * mm});
            skLineSegment(sketch, "E327", {"start": v(-21.39, 42.05) * mm, "end": v(-21.47, 41.37) * mm});
            skLineSegment(sketch, "E328", {"start": v(-21.47, 41.37) * mm, "end": v(-21.59, 40.74) * mm});
            skLineSegment(sketch, "E329", {"start": v(-21.59, 40.74) * mm, "end": v(-21.75, 40.1) * mm});
            skLineSegment(sketch, "E330", {"start": v(-21.75, 40.1) * mm, "end": v(-21.99, 39.46) * mm});
            skLineSegment(sketch, "E331", {"start": v(-21.99, 39.46) * mm, "end": v(-22.23, 38.82) * mm});
            skLineSegment(sketch, "E332", {"start": v(-22.23, 38.82) * mm, "end": v(-22.55, 38.22) * mm});
            skLineSegment(sketch, "E333", {"start": v(-22.55, 38.22) * mm, "end": v(-22.95, 37.66) * mm});
            skLineSegment(sketch, "E334", {"start": v(-22.95, 37.66) * mm, "end": v(-23.35, 37.1) * mm});
            skLineSegment(sketch, "E335", {"start": v(-23.35, 37.1) * mm, "end": v(-23.79, 36.54) * mm});
            skLineSegment(sketch, "E336", {"start": v(-23.79, 36.54) * mm, "end": v(-24.3, 36.06) * mm});
            skLineSegment(sketch, "E337", {"start": v(-24.3, 36.06) * mm, "end": v(-24.82, 35.62) * mm});
            skLineSegment(sketch, "E338", {"start": v(-24.82, 35.62) * mm, "end": v(-25.34, 35.18) * mm});
            skLineSegment(sketch, "E339", {"start": v(-25.34, 35.18) * mm, "end": v(-25.94, 34.82) * mm});
            skLineSegment(sketch, "E340", {"start": v(-25.94, 34.82) * mm, "end": v(-26.58, 34.46) * mm});
            skLineSegment(sketch, "E341", {"start": v(-26.58, 34.46) * mm, "end": v(-27.22, 34.18) * mm});
            skLineSegment(sketch, "E342", {"start": v(-27.22, 34.18) * mm, "end": v(-26.3, 33.86) * mm});
            skLineSegment(sketch, "E343", {"start": v(-26.3, 33.86) * mm, "end": v(-25.42, 33.54) * mm});
            skLineSegment(sketch, "E344", {"start": v(-25.42, 33.54) * mm, "end": v(-24.63, 33.18) * mm});
            skLineSegment(sketch, "E345", {"start": v(-24.63, 33.18) * mm, "end": v(-23.87, 32.74) * mm});
            skLineSegment(sketch, "E346", {"start": v(-23.87, 32.74) * mm, "end": v(-23.15, 32.26) * mm});
            skLineSegment(sketch, "E347", {"start": v(-23.15, 32.26) * mm, "end": v(-22.5, 31.74) * mm});
            skLineSegment(sketch, "E348", {"start": v(-22.5, 31.74) * mm, "end": v(-21.9, 31.18) * mm});
            skLineSegment(sketch, "E349", {"start": v(-21.9, 31.18) * mm, "end": v(-21.35, 30.58) * mm});
            skLineSegment(sketch, "E350", {"start": v(-21.35, 30.58) * mm, "end": v(-20.87, 29.94) * mm});
            skLineSegment(sketch, "E351", {"start": v(-20.87, 29.94) * mm, "end": v(-20.47, 29.26) * mm});
            skLineSegment(sketch, "E352", {"start": v(-20.47, 29.26) * mm, "end": v(-20.1, 28.54) * mm});
            skLineSegment(sketch, "E353", {"start": v(-20.1, 28.54) * mm, "end": v(-19.83, 27.82) * mm});
            skLineSegment(sketch, "E354", {"start": v(-19.83, 27.82) * mm, "end": v(-19.59, 27.06) * mm});
            skLineSegment(sketch, "E355", {"start": v(-19.59, 27.06) * mm, "end": v(-19.43, 26.26) * mm});
            skLineSegment(sketch, "E356", {"start": v(-19.43, 26.26) * mm, "end": v(-19.35, 25.46) * mm});
            skLineSegment(sketch, "E357", {"start": v(-19.35, 25.46) * mm, "end": v(-19.3, 24.63) * mm});
            skLineSegment(sketch, "E358", {"start": v(-19.3, 24.63) * mm, "end": v(-19.3, 23.95) * mm});
            skLineSegment(sketch, "E359", {"start": v(-19.3, 23.95) * mm, "end": v(-19.39, 23.27) * mm});
            skLineSegment(sketch, "E360", {"start": v(-19.39, 23.27) * mm, "end": v(-19.47, 22.63) * mm});
            skLineSegment(sketch, "E361", {"start": v(-19.47, 22.63) * mm, "end": v(-19.63, 21.95) * mm});
            skLineSegment(sketch, "E362", {"start": v(-19.63, 21.95) * mm, "end": v(-19.83, 21.3) * mm});
            skLineSegment(sketch, "E363", {"start": v(-19.83, 21.3) * mm, "end": v(-20.03, 20.67) * mm});
            skLineSegment(sketch, "E364", {"start": v(-20.03, 20.67) * mm, "end": v(-20.3, 20.03) * mm});
            skLineSegment(sketch, "E365", {"start": v(-20.3, 20.03) * mm, "end": v(-20.63, 19.35) * mm});
            skLineSegment(sketch, "E366", {"start": v(-20.63, 19.35) * mm, "end": v(-20.99, 18.75) * mm});
            skLineSegment(sketch, "E367", {"start": v(-20.99, 18.75) * mm, "end": v(-21.35, 18.15) * mm});
            skLineSegment(sketch, "E368", {"start": v(-21.35, 18.15) * mm, "end": v(-21.75, 17.59) * mm});
            skLineSegment(sketch, "E369", {"start": v(-21.75, 17.59) * mm, "end": v(-22.19, 17.07) * mm});
            skLineSegment(sketch, "E370", {"start": v(-22.19, 17.07) * mm, "end": v(-22.67, 16.59) * mm});
            skLineSegment(sketch, "E371", {"start": v(-22.67, 16.59) * mm, "end": v(-23.15, 16.11) * mm});
            skLineSegment(sketch, "E372", {"start": v(-23.15, 16.11) * mm, "end": v(-23.7, 15.71) * mm});
            skLineSegment(sketch, "E373", {"start": v(-23.7, 15.71) * mm, "end": v(-24.27, 15.31) * mm});
            skLineSegment(sketch, "E374", {"start": v(-24.27, 15.31) * mm, "end": v(-24.82, 14.95) * mm});
            skLineSegment(sketch, "E375", {"start": v(-24.82, 14.95) * mm, "end": v(-25.46, 14.6) * mm});
            skLineSegment(sketch, "E376", {"start": v(-25.46, 14.6) * mm, "end": v(-26.14, 14.31) * mm});
            skLineSegment(sketch, "E377", {"start": v(-26.14, 14.31) * mm, "end": v(-26.82, 14.07) * mm});
            skLineSegment(sketch, "E378", {"start": v(-26.82, 14.07) * mm, "end": v(-27.54, 13.87) * mm});
            skLineSegment(sketch, "E379", {"start": v(-27.54, 13.87) * mm, "end": v(-28.3, 13.67) * mm});
            skLineSegment(sketch, "E380", {"start": v(-28.3, 13.67) * mm, "end": v(-29.1, 13.51) * mm});
            skLineSegment(sketch, "E381", {"start": v(-29.1, 13.51) * mm, "end": v(-29.94, 13.43) * mm});
            skLineSegment(sketch, "E382", {"start": v(-29.94, 13.43) * mm, "end": v(-30.54, 13.35) * mm});
            skLineSegment(sketch, "E383", {"start": v(-30.54, 13.35) * mm, "end": v(-31.34, 13.31) * mm});
            skLineSegment(sketch, "E384", {"start": v(-31.34, 13.31) * mm, "end": v(-32.34, 13.27) * mm});
            skLineSegment(sketch, "E385", {"start": v(-32.34, 13.27) * mm, "end": v(-33.54, 13.23) * mm});
            skLineSegment(sketch, "E386", {"start": v(-33.54, 13.23) * mm, "end": v(-34.9, 13.23) * mm});
            skLineSegment(sketch, "E387", {"start": v(-34.9, 13.23) * mm, "end": v(-36.46, 13.2) * mm});
            skLineSegment(sketch, "E388", {"start": v(-36.46, 13.2) * mm, "end": v(-38.18, 13.15) * mm});
            skLineSegment(sketch, "E389", {"start": v(-38.18, 13.15) * mm, "end": v(-40.14, 13.15) * mm});
            skLineSegment(sketch, "E390", {"start": v(-40.14, 13.15) * mm, "end": v(-54.37, 13.15) * mm});
            skLineSegment(sketch, "E391", {"start": v(-54.37, 13.15) * mm, "end": v(-54.37, 52.69) * mm});
            skLineSegment(sketch, "E392", {"start": v(-45.93, 46.13) * mm, "end": v(-45.93, 36.98) * mm});
            skLineSegment(sketch, "E393", {"start": v(-45.93, 36.98) * mm, "end": v(-40.38, 36.98) * mm});
            skLineSegment(sketch, "E394", {"start": v(-40.38, 36.98) * mm, "end": v(-39.22, 36.98) * mm});
            skLineSegment(sketch, "E395", {"start": v(-39.22, 36.98) * mm, "end": v(-38.14, 36.98) * mm});
            skLineSegment(sketch, "E396", {"start": v(-38.14, 36.98) * mm, "end": v(-37.18, 36.98) * mm});
            skLineSegment(sketch, "E397", {"start": v(-37.18, 36.98) * mm, "end": v(-36.38, 37.02) * mm});
            skLineSegment(sketch, "E398", {"start": v(-36.38, 37.02) * mm, "end": v(-35.66, 37.02) * mm});
            skLineSegment(sketch, "E399", {"start": v(-35.66, 37.02) * mm, "end": v(-35.06, 37.06) * mm});
            skLineSegment(sketch, "E400", {"start": v(-35.06, 37.06) * mm, "end": v(-34.58, 37.06) * mm});
            skLineSegment(sketch, "E401", {"start": v(-34.58, 37.06) * mm, "end": v(-34.22, 37.1) * mm});
            skLineSegment(sketch, "E402", {"start": v(-34.22, 37.1) * mm, "end": v(-33.7, 37.18) * mm});
            skLineSegment(sketch, "E403", {"start": v(-33.7, 37.18) * mm, "end": v(-33.22, 37.3) * mm});
            skLineSegment(sketch, "E404", {"start": v(-33.22, 37.3) * mm, "end": v(-32.74, 37.42) * mm});
            skLineSegment(sketch, "E405", {"start": v(-32.74, 37.42) * mm, "end": v(-32.3, 37.58) * mm});
            skLineSegment(sketch, "E406", {"start": v(-32.3, 37.58) * mm, "end": v(-31.9, 37.78) * mm});
            skLineSegment(sketch, "E407", {"start": v(-31.9, 37.78) * mm, "end": v(-31.5, 37.98) * mm});
            skLineSegment(sketch, "E408", {"start": v(-31.5, 37.98) * mm, "end": v(-31.14, 38.26) * mm});
            skLineSegment(sketch, "E409", {"start": v(-31.14, 38.26) * mm, "end": v(-30.82, 38.54) * mm});
            skLineSegment(sketch, "E410", {"start": v(-30.82, 38.54) * mm, "end": v(-30.54, 38.82) * mm});
            skLineSegment(sketch, "E411", {"start": v(-30.54, 38.82) * mm, "end": v(-30.26, 39.14) * mm});
            skLineSegment(sketch, "E412", {"start": v(-30.26, 39.14) * mm, "end": v(-30.06, 39.5) * mm});
            skLineSegment(sketch, "E413", {"start": v(-30.06, 39.5) * mm, "end": v(-29.9, 39.9) * mm});
            skLineSegment(sketch, "E414", {"start": v(-29.9, 39.9) * mm, "end": v(-29.74, 40.3) * mm});
            skLineSegment(sketch, "E415", {"start": v(-29.74, 40.3) * mm, "end": v(-29.66, 40.7) * mm});
            skLineSegment(sketch, "E416", {"start": v(-29.66, 40.7) * mm, "end": v(-29.62, 41.13) * mm});
            skLineSegment(sketch, "E417", {"start": v(-29.62, 41.13) * mm, "end": v(-29.58, 41.61) * mm});
            skLineSegment(sketch, "E418", {"start": v(-29.58, 41.61) * mm, "end": v(-29.58, 42.05) * mm});
            skLineSegment(sketch, "E419", {"start": v(-29.58, 42.05) * mm, "end": v(-29.66, 42.5) * mm});
            skLineSegment(sketch, "E420", {"start": v(-29.66, 42.5) * mm, "end": v(-29.74, 42.9) * mm});
            skLineSegment(sketch, "E421", {"start": v(-29.74, 42.9) * mm, "end": v(-29.86, 43.3) * mm});
            skLineSegment(sketch, "E422", {"start": v(-29.86, 43.3) * mm, "end": v(-29.98, 43.65) * mm});
            skLineSegment(sketch, "E423", {"start": v(-29.98, 43.65) * mm, "end": v(-30.18, 43.97) * mm});
            skLineSegment(sketch, "E424", {"start": v(-30.18, 43.97) * mm, "end": v(-30.38, 44.3) * mm});
            skLineSegment(sketch, "E425", {"start": v(-30.38, 44.3) * mm, "end": v(-30.66, 44.61) * mm});
            skLineSegment(sketch, "E426", {"start": v(-30.66, 44.61) * mm, "end": v(-30.94, 44.85) * mm});
            skLineSegment(sketch, "E427", {"start": v(-30.94, 44.85) * mm, "end": v(-31.26, 45.1) * mm});
            skLineSegment(sketch, "E428", {"start": v(-31.26, 45.1) * mm, "end": v(-31.62, 45.33) * mm});
            skLineSegment(sketch, "E429", {"start": v(-31.62, 45.33) * mm, "end": v(-31.98, 45.53) * mm});
            skLineSegment(sketch, "E430", {"start": v(-31.98, 45.53) * mm, "end": v(-32.38, 45.65) * mm});
            skLineSegment(sketch, "E431", {"start": v(-32.38, 45.65) * mm, "end": v(-32.86, 45.81) * mm});
            skLineSegment(sketch, "E432", {"start": v(-32.86, 45.81) * mm, "end": v(-33.34, 45.9) * mm});
            skLineSegment(sketch, "E433", {"start": v(-33.34, 45.9) * mm, "end": v(-33.82, 45.97) * mm});
            skLineSegment(sketch, "E434", {"start": v(-33.82, 45.97) * mm, "end": v(-34.22, 46.01) * mm});
            skLineSegment(sketch, "E435", {"start": v(-34.22, 46.01) * mm, "end": v(-34.74, 46.05) * mm});
            skLineSegment(sketch, "E436", {"start": v(-34.74, 46.05) * mm, "end": v(-35.46, 46.05) * mm});
            skLineSegment(sketch, "E437", {"start": v(-35.46, 46.05) * mm, "end": v(-36.26, 46.1) * mm});
            skLineSegment(sketch, "E438", {"start": v(-36.26, 46.1) * mm, "end": v(-37.26, 46.1) * mm});
            skLineSegment(sketch, "E439", {"start": v(-37.26, 46.1) * mm, "end": v(-38.38, 46.1) * mm});
            skLineSegment(sketch, "E440", {"start": v(-38.38, 46.1) * mm, "end": v(-39.66, 46.1) * mm});
            skLineSegment(sketch, "E441", {"start": v(-39.66, 46.1) * mm, "end": v(-41.06, 46.13) * mm});
            skLineSegment(sketch, "E442", {"start": v(-41.06, 46.13) * mm, "end": v(-45.93, 46.13) * mm});
            skLineSegment(sketch, "E443", {"start": v(-45.93, 30.38) * mm, "end": v(-45.93, 19.83) * mm});
            skLineSegment(sketch, "E444", {"start": v(-45.93, 19.83) * mm, "end": v(-38.1, 19.83) * mm});
            skLineSegment(sketch, "E445", {"start": v(-38.1, 19.83) * mm, "end": v(-36.02, 19.83) * mm});
            skLineSegment(sketch, "E446", {"start": v(-36.02, 19.83) * mm, "end": v(-34.34, 19.87) * mm});
            skLineSegment(sketch, "E447", {"start": v(-34.34, 19.87) * mm, "end": v(-33.1, 19.95) * mm});
            skLineSegment(sketch, "E448", {"start": v(-33.1, 19.95) * mm, "end": v(-32.3, 20.07) * mm});
            skLineSegment(sketch, "E449", {"start": v(-32.3, 20.07) * mm, "end": v(-31.82, 20.15) * mm});
            skLineSegment(sketch, "E450", {"start": v(-31.82, 20.15) * mm, "end": v(-31.38, 20.27) * mm});
            skLineSegment(sketch, "E451", {"start": v(-31.38, 20.27) * mm, "end": v(-30.98, 20.43) * mm});
            skLineSegment(sketch, "E452", {"start": v(-30.98, 20.43) * mm, "end": v(-30.58, 20.63) * mm});
            skLineSegment(sketch, "E453", {"start": v(-30.58, 20.63) * mm, "end": v(-30.22, 20.83) * mm});
            skLineSegment(sketch, "E454", {"start": v(-30.22, 20.83) * mm, "end": v(-29.86, 21.07) * mm});
            skLineSegment(sketch, "E455", {"start": v(-29.86, 21.07) * mm, "end": v(-29.54, 21.35) * mm});
            skLineSegment(sketch, "E456", {"start": v(-29.54, 21.35) * mm, "end": v(-29.22, 21.63) * mm});
            skLineSegment(sketch, "E457", {"start": v(-29.22, 21.63) * mm, "end": v(-28.94, 21.95) * mm});
            skLineSegment(sketch, "E458", {"start": v(-28.94, 21.95) * mm, "end": v(-28.7, 22.3) * mm});
            skLineSegment(sketch, "E459", {"start": v(-28.7, 22.3) * mm, "end": v(-28.5, 22.7) * mm});
            skLineSegment(sketch, "E460", {"start": v(-28.5, 22.7) * mm, "end": v(-28.34, 23.1) * mm});
            skLineSegment(sketch, "E461", {"start": v(-28.34, 23.1) * mm, "end": v(-28.18, 23.55) * mm});
            skLineSegment(sketch, "E462", {"start": v(-28.18, 23.55) * mm, "end": v(-28.1, 23.99) * mm});
            skLineSegment(sketch, "E463", {"start": v(-28.1, 23.99) * mm, "end": v(-28.06, 24.47) * mm});
            skLineSegment(sketch, "E464", {"start": v(-28.06, 24.47) * mm, "end": v(-28.02, 24.98) * mm});
            skLineSegment(sketch, "E465", {"start": v(-28.02, 24.98) * mm, "end": v(-28.06, 25.42) * mm});
            skLineSegment(sketch, "E466", {"start": v(-28.06, 25.42) * mm, "end": v(-28.1, 25.86) * mm});
            skLineSegment(sketch, "E467", {"start": v(-28.1, 25.86) * mm, "end": v(-28.18, 26.26) * mm});
            skLineSegment(sketch, "E468", {"start": v(-28.18, 26.26) * mm, "end": v(-28.26, 26.62) * mm});
            skLineSegment(sketch, "E469", {"start": v(-28.26, 26.62) * mm, "end": v(-28.38, 27.02) * mm});
            skLineSegment(sketch, "E470", {"start": v(-28.38, 27.02) * mm, "end": v(-28.54, 27.34) * mm});
            skLineSegment(sketch, "E471", {"start": v(-28.54, 27.34) * mm, "end": v(-28.74, 27.7) * mm});
            skLineSegment(sketch, "E472", {"start": v(-28.74, 27.7) * mm, "end": v(-28.94, 28.02) * mm});
            skLineSegment(sketch, "E473", {"start": v(-28.94, 28.02) * mm, "end": v(-29.18, 28.3) * mm});
            skLineSegment(sketch, "E474", {"start": v(-29.18, 28.3) * mm, "end": v(-29.46, 28.58) * mm});
            skLineSegment(sketch, "E475", {"start": v(-29.46, 28.58) * mm, "end": v(-29.74, 28.86) * mm});
            skLineSegment(sketch, "E476", {"start": v(-29.74, 28.86) * mm, "end": v(-30.06, 29.1) * mm});
            skLineSegment(sketch, "E477", {"start": v(-30.06, 29.1) * mm, "end": v(-30.42, 29.3) * mm});
            skLineSegment(sketch, "E478", {"start": v(-30.42, 29.3) * mm, "end": v(-30.78, 29.5) * mm});
            skLineSegment(sketch, "E479", {"start": v(-30.78, 29.5) * mm, "end": v(-31.18, 29.66) * mm});
            skLineSegment(sketch, "E480", {"start": v(-31.18, 29.66) * mm, "end": v(-31.58, 29.82) * mm});
            skLineSegment(sketch, "E481", {"start": v(-31.58, 29.82) * mm, "end": v(-32.1, 29.94) * mm});
            skLineSegment(sketch, "E482", {"start": v(-32.1, 29.94) * mm, "end": v(-32.7, 30.06) * mm});
            skLineSegment(sketch, "E483", {"start": v(-32.7, 30.06) * mm, "end": v(-33.46, 30.18) * mm});
            skLineSegment(sketch, "E484", {"start": v(-33.46, 30.18) * mm, "end": v(-34.34, 30.26) * mm});
            skLineSegment(sketch, "E485", {"start": v(-34.34, 30.26) * mm, "end": v(-35.34, 30.3) * mm});
            skLineSegment(sketch, "E486", {"start": v(-35.34, 30.3) * mm, "end": v(-36.46, 30.34) * mm});
            skLineSegment(sketch, "E487", {"start": v(-36.46, 30.34) * mm, "end": v(-37.7, 30.38) * mm});
            skLineSegment(sketch, "E488", {"start": v(-37.7, 30.38) * mm, "end": v(-39.1, 30.38) * mm});
            skLineSegment(sketch, "E489", {"start": v(-39.1, 30.38) * mm, "end": v(-45.93, 30.38) * mm});
            skLineSegment(sketch, "E490", {"start": v(0.48, 6.92) * mm, "end": v(18.03, -3.24) * mm});
            skLineSegment(sketch, "E491", {"start": v(18.03, -3.24) * mm, "end": v(35.58, -13.35) * mm});
            skLineSegment(sketch, "E492", {"start": v(35.58, -13.35) * mm, "end": v(35.58, -33.62) * mm});
            skLineSegment(sketch, "E493", {"start": v(35.58, -33.62) * mm, "end": v(35.58, -53.89) * mm});
            skLineSegment(sketch, "E494", {"start": v(35.58, -53.89) * mm, "end": v(18.03, -64) * mm});
            skLineSegment(sketch, "E495", {"start": v(18.03, -64) * mm, "end": v(0.48, -74.11) * mm});
            skLineSegment(sketch, "E496", {"start": v(0.48, -74.11) * mm, "end": v(-17.07, -64) * mm});
            skLineSegment(sketch, "E497", {"start": v(-17.07, -64) * mm, "end": v(-34.58, -53.89) * mm});
            skLineSegment(sketch, "E498", {"start": v(-34.58, -53.89) * mm, "end": v(-34.58, -33.62) * mm});
            skLineSegment(sketch, "E499", {"start": v(-34.58, -33.62) * mm, "end": v(-34.58, -13.35) * mm});
            skLineSegment(sketch, "E500", {"start": v(-34.58, -13.35) * mm, "end": v(-17.07, -3.24) * mm});
            skLineSegment(sketch, "E501", {"start": v(-17.07, -3.24) * mm, "end": v(0.48, 6.92) * mm});
            skLineSegment(sketch, "E502", {"start": v(0.68, -3.4) * mm, "end": v(2.28, -3.44) * mm});
            skLineSegment(sketch, "E503", {"start": v(2.28, -3.44) * mm, "end": v(3.88, -3.56) * mm});
            skLineSegment(sketch, "E504", {"start": v(3.88, -3.56) * mm, "end": v(5.44, -3.76) * mm});
            skLineSegment(sketch, "E505", {"start": v(5.44, -3.76) * mm, "end": v(6.96, -4.04) * mm});
            skLineSegment(sketch, "E506", {"start": v(6.96, -4.04) * mm, "end": v(8.47, -4.36) * mm});
            skLineSegment(sketch, "E507", {"start": v(8.47, -4.36) * mm, "end": v(9.95, -4.8) * mm});
            skLineSegment(sketch, "E508", {"start": v(9.95, -4.8) * mm, "end": v(11.4, -5.28) * mm});
            skLineSegment(sketch, "E509", {"start": v(11.4, -5.28) * mm, "end": v(12.8, -5.84) * mm});
            skLineSegment(sketch, "E510", {"start": v(12.8, -5.84) * mm, "end": v(14.2, -6.48) * mm});
            skLineSegment(sketch, "E511", {"start": v(14.2, -6.48) * mm, "end": v(15.55, -7.16) * mm});
            skLineSegment(sketch, "E512", {"start": v(15.55, -7.16) * mm, "end": v(16.83, -7.92) * mm});
            skLineSegment(sketch, "E513", {"start": v(16.83, -7.92) * mm, "end": v(18.1, -8.71) * mm});
            skLineSegment(sketch, "E514", {"start": v(18.1, -8.71) * mm, "end": v(19.3, -9.6) * mm});
            skLineSegment(sketch, "E515", {"start": v(19.3, -9.6) * mm, "end": v(20.5, -10.51) * mm});
            skLineSegment(sketch, "E516", {"start": v(20.5, -10.51) * mm, "end": v(21.63, -11.47) * mm});
            skLineSegment(sketch, "E517", {"start": v(21.63, -11.47) * mm, "end": v(22.7, -12.51) * mm});
            skLineSegment(sketch, "E518", {"start": v(22.7, -12.51) * mm, "end": v(23.75, -13.6) * mm});
            skLineSegment(sketch, "E519", {"start": v(23.75, -13.6) * mm, "end": v(24.7, -14.71) * mm});
            skLineSegment(sketch, "E520", {"start": v(24.7, -14.71) * mm, "end": v(25.62, -15.91) * mm});
            skLineSegment(sketch, "E521", {"start": v(25.62, -15.91) * mm, "end": v(26.5, -17.1) * mm});
            skLineSegment(sketch, "E522", {"start": v(26.5, -17.1) * mm, "end": v(27.3, -18.39) * mm});
            skLineSegment(sketch, "E523", {"start": v(27.3, -18.39) * mm, "end": v(28.06, -19.7) * mm});
            skLineSegment(sketch, "E524", {"start": v(28.06, -19.7) * mm, "end": v(28.74, -21.03) * mm});
            skLineSegment(sketch, "E525", {"start": v(28.74, -21.03) * mm, "end": v(29.38, -22.43) * mm});
            skLineSegment(sketch, "E526", {"start": v(29.38, -22.43) * mm, "end": v(29.94, -23.83) * mm});
            skLineSegment(sketch, "E527", {"start": v(29.94, -23.83) * mm, "end": v(30.42, -25.26) * mm});
            skLineSegment(sketch, "E528", {"start": v(30.42, -25.26) * mm, "end": v(30.86, -26.74) * mm});
            skLineSegment(sketch, "E529", {"start": v(30.86, -26.74) * mm, "end": v(31.18, -28.26) * mm});
            skLineSegment(sketch, "E530", {"start": v(31.18, -28.26) * mm, "end": v(31.46, -29.78) * mm});
            skLineSegment(sketch, "E531", {"start": v(31.46, -29.78) * mm, "end": v(31.66, -31.34) * mm});
            skLineSegment(sketch, "E532", {"start": v(31.66, -31.34) * mm, "end": v(31.78, -32.94) * mm});
            skLineSegment(sketch, "E533", {"start": v(31.78, -32.94) * mm, "end": v(31.82, -34.54) * mm});
            skLineSegment(sketch, "E534", {"start": v(31.82, -34.54) * mm, "end": v(31.78, -36.14) * mm});
            skLineSegment(sketch, "E535", {"start": v(31.78, -36.14) * mm, "end": v(31.66, -37.7) * mm});
            skLineSegment(sketch, "E536", {"start": v(31.66, -37.7) * mm, "end": v(31.46, -39.26) * mm});
            skLineSegment(sketch, "E537", {"start": v(31.46, -39.26) * mm, "end": v(31.18, -40.82) * mm});
            skLineSegment(sketch, "E538", {"start": v(31.18, -40.82) * mm, "end": v(30.86, -42.3) * mm});
            skLineSegment(sketch, "E539", {"start": v(30.86, -42.3) * mm, "end": v(30.42, -43.77) * mm});
            skLineSegment(sketch, "E540", {"start": v(30.42, -43.77) * mm, "end": v(29.94, -45.25) * mm});
            skLineSegment(sketch, "E541", {"start": v(29.94, -45.25) * mm, "end": v(29.38, -46.65) * mm});
            skLineSegment(sketch, "E542", {"start": v(29.38, -46.65) * mm, "end": v(28.74, -48.05) * mm});
            skLineSegment(sketch, "E543", {"start": v(28.74, -48.05) * mm, "end": v(28.06, -49.37) * mm});
            skLineSegment(sketch, "E544", {"start": v(28.06, -49.37) * mm, "end": v(27.3, -50.69) * mm});
            skLineSegment(sketch, "E545", {"start": v(27.3, -50.69) * mm, "end": v(26.5, -51.93) * mm});
            skLineSegment(sketch, "E546", {"start": v(26.5, -51.93) * mm, "end": v(25.62, -53.17) * mm});
            skLineSegment(sketch, "E547", {"start": v(25.62, -53.17) * mm, "end": v(24.7, -54.33) * mm});
            skLineSegment(sketch, "E548", {"start": v(24.7, -54.33) * mm, "end": v(23.75, -55.49) * mm});
            skLineSegment(sketch, "E549", {"start": v(23.75, -55.49) * mm, "end": v(22.7, -56.57) * mm});
            skLineSegment(sketch, "E550", {"start": v(22.7, -56.57) * mm, "end": v(21.63, -57.56) * mm});
            skLineSegment(sketch, "E551", {"start": v(21.63, -57.56) * mm, "end": v(20.5, -58.56) * mm});
            skLineSegment(sketch, "E552", {"start": v(20.5, -58.56) * mm, "end": v(19.3, -59.48) * mm});
            skLineSegment(sketch, "E553", {"start": v(19.3, -59.48) * mm, "end": v(18.1, -60.36) * mm});
            skLineSegment(sketch, "E554", {"start": v(18.1, -60.36) * mm, "end": v(16.83, -61.16) * mm});
            skLineSegment(sketch, "E555", {"start": v(16.83, -61.16) * mm, "end": v(15.55, -61.92) * mm});
            skLineSegment(sketch, "E556", {"start": v(15.55, -61.92) * mm, "end": v(14.2, -62.6) * mm});
            skLineSegment(sketch, "E557", {"start": v(14.2, -62.6) * mm, "end": v(12.8, -63.24) * mm});
            skLineSegment(sketch, "E558", {"start": v(12.8, -63.24) * mm, "end": v(11.4, -63.8) * mm});
            skLineSegment(sketch, "E559", {"start": v(11.4, -63.8) * mm, "end": v(9.95, -64.28) * mm});
            skLineSegment(sketch, "E560", {"start": v(9.95, -64.28) * mm, "end": v(8.47, -64.68) * mm});
            skLineSegment(sketch, "E561", {"start": v(8.47, -64.68) * mm, "end": v(6.96, -65.04) * mm});
            skLineSegment(sketch, "E562", {"start": v(6.96, -65.04) * mm, "end": v(5.44, -65.32) * mm});
            skLineSegment(sketch, "E563", {"start": v(5.44, -65.32) * mm, "end": v(3.88, -65.52) * mm});
            skLineSegment(sketch, "E564", {"start": v(3.88, -65.52) * mm, "end": v(2.28, -65.64) * mm});
            skLineSegment(sketch, "E565", {"start": v(2.28, -65.64) * mm, "end": v(0.68, -65.68) * mm});
            skLineSegment(sketch, "E566", {"start": v(0.68, -65.68) * mm, "end": v(-0.92, -65.64) * mm});
            skLineSegment(sketch, "E567", {"start": v(-0.92, -65.64) * mm, "end": v(-2.48, -65.52) * mm});
            skLineSegment(sketch, "E568", {"start": v(-2.48, -65.52) * mm, "end": v(-4.04, -65.32) * mm});
            skLineSegment(sketch, "E569", {"start": v(-4.04, -65.32) * mm, "end": v(-5.6, -65.04) * mm});
            skLineSegment(sketch, "E570", {"start": v(-5.6, -65.04) * mm, "end": v(-7.08, -64.68) * mm});
            skLineSegment(sketch, "E571", {"start": v(-7.08, -64.68) * mm, "end": v(-8.55, -64.28) * mm});
            skLineSegment(sketch, "E572", {"start": v(-8.55, -64.28) * mm, "end": v(-10.03, -63.8) * mm});
            skLineSegment(sketch, "E573", {"start": v(-10.03, -63.8) * mm, "end": v(-11.43, -63.24) * mm});
            skLineSegment(sketch, "E574", {"start": v(-11.43, -63.24) * mm, "end": v(-12.8, -62.6) * mm});
            skLineSegment(sketch, "E575", {"start": v(-12.8, -62.6) * mm, "end": v(-14.15, -61.92) * mm});
            skLineSegment(sketch, "E576", {"start": v(-14.15, -61.92) * mm, "end": v(-15.47, -61.16) * mm});
            skLineSegment(sketch, "E577", {"start": v(-15.47, -61.16) * mm, "end": v(-16.7, -60.36) * mm});
            skLineSegment(sketch, "E578", {"start": v(-16.7, -60.36) * mm, "end": v(-17.95, -59.48) * mm});
            skLineSegment(sketch, "E579", {"start": v(-17.95, -59.48) * mm, "end": v(-19.1, -58.56) * mm});
            skLineSegment(sketch, "E580", {"start": v(-19.1, -58.56) * mm, "end": v(-20.23, -57.56) * mm});
            skLineSegment(sketch, "E581", {"start": v(-20.23, -57.56) * mm, "end": v(-21.35, -56.57) * mm});
            skLineSegment(sketch, "E582", {"start": v(-21.35, -56.57) * mm, "end": v(-22.35, -55.49) * mm});
            skLineSegment(sketch, "E583", {"start": v(-22.35, -55.49) * mm, "end": v(-23.35, -54.33) * mm});
            skLineSegment(sketch, "E584", {"start": v(-23.35, -54.33) * mm, "end": v(-24.27, -53.17) * mm});
            skLineSegment(sketch, "E585", {"start": v(-24.27, -53.17) * mm, "end": v(-25.14, -51.93) * mm});
            skLineSegment(sketch, "E586", {"start": v(-25.14, -51.93) * mm, "end": v(-25.94, -50.69) * mm});
            skLineSegment(sketch, "E587", {"start": v(-25.94, -50.69) * mm, "end": v(-26.7, -49.37) * mm});
            skLineSegment(sketch, "E588", {"start": v(-26.7, -49.37) * mm, "end": v(-27.38, -48.05) * mm});
            skLineSegment(sketch, "E589", {"start": v(-27.38, -48.05) * mm, "end": v(-28.02, -46.65) * mm});
            skLineSegment(sketch, "E590", {"start": v(-28.02, -46.65) * mm, "end": v(-28.54, -45.25) * mm});
            skLineSegment(sketch, "E591", {"start": v(-28.54, -45.25) * mm, "end": v(-29.06, -43.77) * mm});
            skLineSegment(sketch, "E592", {"start": v(-29.06, -43.77) * mm, "end": v(-29.46, -42.3) * mm});
            skLineSegment(sketch, "E593", {"start": v(-29.46, -42.3) * mm, "end": v(-29.82, -40.82) * mm});
            skLineSegment(sketch, "E594", {"start": v(-29.82, -40.82) * mm, "end": v(-30.1, -39.26) * mm});
            skLineSegment(sketch, "E595", {"start": v(-30.1, -39.26) * mm, "end": v(-30.3, -37.7) * mm});
            skLineSegment(sketch, "E596", {"start": v(-30.3, -37.7) * mm, "end": v(-30.42, -36.14) * mm});
            skLineSegment(sketch, "E597", {"start": v(-30.42, -36.14) * mm, "end": v(-30.46, -34.54) * mm});
            skLineSegment(sketch, "E598", {"start": v(-30.46, -34.54) * mm, "end": v(-30.42, -32.94) * mm});
            skLineSegment(sketch, "E599", {"start": v(-30.42, -32.94) * mm, "end": v(-30.3, -31.34) * mm});
            skLineSegment(sketch, "E600", {"start": v(-30.3, -31.34) * mm, "end": v(-30.1, -29.78) * mm});
            skLineSegment(sketch, "E601", {"start": v(-30.1, -29.78) * mm, "end": v(-29.82, -28.26) * mm});
            skLineSegment(sketch, "E602", {"start": v(-29.82, -28.26) * mm, "end": v(-29.46, -26.74) * mm});
            skLineSegment(sketch, "E603", {"start": v(-29.46, -26.74) * mm, "end": v(-29.06, -25.26) * mm});
            skLineSegment(sketch, "E604", {"start": v(-29.06, -25.26) * mm, "end": v(-28.54, -23.83) * mm});
            skLineSegment(sketch, "E605", {"start": v(-28.54, -23.83) * mm, "end": v(-28.02, -22.43) * mm});
            skLineSegment(sketch, "E606", {"start": v(-28.02, -22.43) * mm, "end": v(-27.38, -21.03) * mm});
            skLineSegment(sketch, "E607", {"start": v(-27.38, -21.03) * mm, "end": v(-26.7, -19.7) * mm});
            skLineSegment(sketch, "E608", {"start": v(-26.7, -19.7) * mm, "end": v(-25.94, -18.39) * mm});
            skLineSegment(sketch, "E609", {"start": v(-25.94, -18.39) * mm, "end": v(-25.14, -17.1) * mm});
            skLineSegment(sketch, "E610", {"start": v(-25.14, -17.1) * mm, "end": v(-24.27, -15.91) * mm});
            skLineSegment(sketch, "E611", {"start": v(-24.27, -15.91) * mm, "end": v(-23.35, -14.71) * mm});
            skLineSegment(sketch, "E612", {"start": v(-23.35, -14.71) * mm, "end": v(-22.35, -13.6) * mm});
            skLineSegment(sketch, "E613", {"start": v(-22.35, -13.6) * mm, "end": v(-21.35, -12.51) * mm});
            skLineSegment(sketch, "E614", {"start": v(-21.35, -12.51) * mm, "end": v(-20.23, -11.47) * mm});
            skLineSegment(sketch, "E615", {"start": v(-20.23, -11.47) * mm, "end": v(-19.1, -10.51) * mm});
            skLineSegment(sketch, "E616", {"start": v(-19.1, -10.51) * mm, "end": v(-17.95, -9.6) * mm});
            skLineSegment(sketch, "E617", {"start": v(-17.95, -9.6) * mm, "end": v(-16.7, -8.71) * mm});
            skLineSegment(sketch, "E618", {"start": v(-16.7, -8.71) * mm, "end": v(-15.47, -7.92) * mm});
            skLineSegment(sketch, "E619", {"start": v(-15.47, -7.92) * mm, "end": v(-14.15, -7.16) * mm});
            skLineSegment(sketch, "E620", {"start": v(-14.15, -7.16) * mm, "end": v(-12.8, -6.48) * mm});
            skLineSegment(sketch, "E621", {"start": v(-12.8, -6.48) * mm, "end": v(-11.43, -5.84) * mm});
            skLineSegment(sketch, "E622", {"start": v(-11.43, -5.84) * mm, "end": v(-10.03, -5.28) * mm});
            skLineSegment(sketch, "E623", {"start": v(-10.03, -5.28) * mm, "end": v(-8.55, -4.8) * mm});
            skLineSegment(sketch, "E624", {"start": v(-8.55, -4.8) * mm, "end": v(-7.08, -4.36) * mm});
            skLineSegment(sketch, "E625", {"start": v(-7.08, -4.36) * mm, "end": v(-5.6, -4.04) * mm});
            skLineSegment(sketch, "E626", {"start": v(-5.6, -4.04) * mm, "end": v(-4.04, -3.76) * mm});
            skLineSegment(sketch, "E627", {"start": v(-4.04, -3.76) * mm, "end": v(-2.48, -3.56) * mm});
            skLineSegment(sketch, "E628", {"start": v(-2.48, -3.56) * mm, "end": v(-0.92, -3.44) * mm});
            skLineSegment(sketch, "E629", {"start": v(-0.92, -3.44) * mm, "end": v(0.68, -3.4) * mm});
            skLineSegment(sketch, "E630", {"start": v(-12.15, -53.97) * mm, "end": v(-12.15, -14.43) * mm});
            skLineSegment(sketch, "E631", {"start": v(-12.15, -14.43) * mm, "end": v(1.4, -14.43) * mm});
            skLineSegment(sketch, "E632", {"start": v(1.4, -14.43) * mm, "end": v(3.28, -14.43) * mm});
            skLineSegment(sketch, "E633", {"start": v(3.28, -14.43) * mm, "end": v(4.92, -14.47) * mm});
            skLineSegment(sketch, "E634", {"start": v(4.92, -14.47) * mm, "end": v(6.44, -14.51) * mm});
            skLineSegment(sketch, "E635", {"start": v(6.44, -14.51) * mm, "end": v(7.8, -14.6) * mm});
            skLineSegment(sketch, "E636", {"start": v(7.8, -14.6) * mm, "end": v(8.95, -14.67) * mm});
            skLineSegment(sketch, "E637", {"start": v(8.95, -14.67) * mm, "end": v(9.95, -14.8) * mm});
            skLineSegment(sketch, "E638", {"start": v(9.95, -14.8) * mm, "end": v(10.8, -14.91) * mm});
            skLineSegment(sketch, "E639", {"start": v(10.8, -14.91) * mm, "end": v(11.47, -15.03) * mm});
            skLineSegment(sketch, "E640", {"start": v(11.47, -15.03) * mm, "end": v(12.35, -15.27) * mm});
            skLineSegment(sketch, "E641", {"start": v(12.35, -15.27) * mm, "end": v(13.2, -15.6) * mm});
            skLineSegment(sketch, "E642", {"start": v(13.2, -15.6) * mm, "end": v(14, -16) * mm});
            skLineSegment(sketch, "E643", {"start": v(14, -16) * mm, "end": v(14.8, -16.43) * mm});
            skLineSegment(sketch, "E644", {"start": v(14.8, -16.43) * mm, "end": v(15.51, -16.95) * mm});
            skLineSegment(sketch, "E645", {"start": v(15.51, -16.95) * mm, "end": v(16.23, -17.55) * mm});
            skLineSegment(sketch, "E646", {"start": v(16.23, -17.55) * mm, "end": v(16.87, -18.19) * mm});
            skLineSegment(sketch, "E647", {"start": v(16.87, -18.19) * mm, "end": v(17.5, -18.9) * mm});
            skLineSegment(sketch, "E648", {"start": v(17.5, -18.9) * mm, "end": v(17.79, -19.27) * mm});
            skLineSegment(sketch, "E649", {"start": v(17.79, -19.27) * mm, "end": v(18.07, -19.67) * mm});
            skLineSegment(sketch, "E650", {"start": v(18.07, -19.67) * mm, "end": v(18.35, -20.07) * mm});
            skLineSegment(sketch, "E651", {"start": v(18.35, -20.07) * mm, "end": v(18.55, -20.5) * mm});
            skLineSegment(sketch, "E652", {"start": v(18.55, -20.5) * mm, "end": v(18.79, -20.95) * mm});
            skLineSegment(sketch, "E653", {"start": v(18.79, -20.95) * mm, "end": v(18.99, -21.39) * mm});
            skLineSegment(sketch, "E654", {"start": v(18.99, -21.39) * mm, "end": v(19.15, -21.83) * mm});
            skLineSegment(sketch, "E655", {"start": v(19.15, -21.83) * mm, "end": v(19.3, -22.3) * mm});
            skLineSegment(sketch, "E656", {"start": v(19.3, -22.3) * mm, "end": v(19.47, -22.79) * mm});
            skLineSegment(sketch, "E657", {"start": v(19.47, -22.79) * mm, "end": v(19.59, -23.3) * mm});
            skLineSegment(sketch, "E658", {"start": v(19.59, -23.3) * mm, "end": v(19.7, -23.83) * mm});
            skLineSegment(sketch, "E659", {"start": v(19.7, -23.83) * mm, "end": v(19.79, -24.35) * mm});
            skLineSegment(sketch, "E660", {"start": v(19.79, -24.35) * mm, "end": v(19.9, -25.46) * mm});
            skLineSegment(sketch, "E661", {"start": v(19.9, -25.46) * mm, "end": v(19.95, -26.58) * mm});
            skLineSegment(sketch, "E662", {"start": v(19.95, -26.58) * mm, "end": v(19.9, -27.5) * mm});
            skLineSegment(sketch, "E663", {"start": v(19.9, -27.5) * mm, "end": v(19.83, -28.34) * mm});
            skLineSegment(sketch, "E664", {"start": v(19.83, -28.34) * mm, "end": v(19.75, -29.18) * mm});
            skLineSegment(sketch, "E665", {"start": v(19.75, -29.18) * mm, "end": v(19.59, -29.94) * mm});
            skLineSegment(sketch, "E666", {"start": v(19.59, -29.94) * mm, "end": v(19.39, -30.7) * mm});
            skLineSegment(sketch, "E667", {"start": v(19.39, -30.7) * mm, "end": v(19.15, -31.42) * mm});
            skLineSegment(sketch, "E668", {"start": v(19.15, -31.42) * mm, "end": v(18.87, -32.1) * mm});
            skLineSegment(sketch, "E669", {"start": v(18.87, -32.1) * mm, "end": v(18.5, -32.7) * mm});
            skLineSegment(sketch, "E670", {"start": v(18.5, -32.7) * mm, "end": v(18.15, -33.34) * mm});
            skLineSegment(sketch, "E671", {"start": v(18.15, -33.34) * mm, "end": v(17.79, -33.9) * mm});
            skLineSegment(sketch, "E672", {"start": v(17.79, -33.9) * mm, "end": v(17.39, -34.42) * mm});
            skLineSegment(sketch, "E673", {"start": v(17.39, -34.42) * mm, "end": v(16.95, -34.94) * mm});
            skLineSegment(sketch, "E674", {"start": v(16.95, -34.94) * mm, "end": v(16.47, -35.42) * mm});
            skLineSegment(sketch, "E675", {"start": v(16.47, -35.42) * mm, "end": v(16, -35.86) * mm});
            skLineSegment(sketch, "E676", {"start": v(16, -35.86) * mm, "end": v(15.51, -36.26) * mm});
            skLineSegment(sketch, "E677", {"start": v(15.51, -36.26) * mm, "end": v(14.95, -36.62) * mm});
            skLineSegment(sketch, "E678", {"start": v(14.95, -36.62) * mm, "end": v(14.43, -36.98) * mm});
            skLineSegment(sketch, "E679", {"start": v(14.43, -36.98) * mm, "end": v(13.87, -37.26) * mm});
            skLineSegment(sketch, "E680", {"start": v(13.87, -37.26) * mm, "end": v(13.35, -37.54) * mm});
            skLineSegment(sketch, "E681", {"start": v(13.35, -37.54) * mm, "end": v(12.8, -37.78) * mm});
            skLineSegment(sketch, "E682", {"start": v(12.8, -37.78) * mm, "end": v(12.23, -38.02) * mm});
            skLineSegment(sketch, "E683", {"start": v(12.23, -38.02) * mm, "end": v(11.71, -38.22) * mm});
            skLineSegment(sketch, "E684", {"start": v(11.71, -38.22) * mm, "end": v(11.15, -38.38) * mm});
            skLineSegment(sketch, "E685", {"start": v(11.15, -38.38) * mm, "end": v(10.6, -38.5) * mm});
            skLineSegment(sketch, "E686", {"start": v(10.6, -38.5) * mm, "end": v(9.8, -38.62) * mm});
            skLineSegment(sketch, "E687", {"start": v(9.8, -38.62) * mm, "end": v(8.91, -38.74) * mm});
            skLineSegment(sketch, "E688", {"start": v(8.91, -38.74) * mm, "end": v(7.96, -38.86) * mm});
            skLineSegment(sketch, "E689", {"start": v(7.96, -38.86) * mm, "end": v(6.88, -38.94) * mm});
            skLineSegment(sketch, "E690", {"start": v(6.88, -38.94) * mm, "end": v(5.76, -38.98) * mm});
            skLineSegment(sketch, "E691", {"start": v(5.76, -38.98) * mm, "end": v(4.52, -39.02) * mm});
            skLineSegment(sketch, "E692", {"start": v(4.52, -39.02) * mm, "end": v(3.2, -39.06) * mm});
            skLineSegment(sketch, "E693", {"start": v(3.2, -39.06) * mm, "end": v(1.8, -39.06) * mm});
            skLineSegment(sketch, "E694", {"start": v(1.8, -39.06) * mm, "end": v(-3.68, -39.06) * mm});
            skLineSegment(sketch, "E695", {"start": v(-3.68, -39.06) * mm, "end": v(-3.68, -53.97) * mm});
            skLineSegment(sketch, "E696", {"start": v(-3.68, -53.97) * mm, "end": v(-12.15, -53.97) * mm});
            skLineSegment(sketch, "E697", {"start": v(-3.68, -21.1) * mm, "end": v(-3.68, -32.34) * mm});
            skLineSegment(sketch, "E698", {"start": v(-3.68, -32.34) * mm, "end": v(0.92, -32.34) * mm});
            skLineSegment(sketch, "E699", {"start": v(0.92, -32.34) * mm, "end": v(2.12, -32.34) * mm});
            skLineSegment(sketch, "E700", {"start": v(2.12, -32.34) * mm, "end": v(3.24, -32.3) * mm});
            skLineSegment(sketch, "E701", {"start": v(3.24, -32.3) * mm, "end": v(4.2, -32.26) * mm});
            skLineSegment(sketch, "E702", {"start": v(4.2, -32.26) * mm, "end": v(5.12, -32.18) * mm});
            skLineSegment(sketch, "E703", {"start": v(5.12, -32.18) * mm, "end": v(5.88, -32.1) * mm});
            skLineSegment(sketch, "E704", {"start": v(5.88, -32.1) * mm, "end": v(6.56, -31.98) * mm});
            skLineSegment(sketch, "E705", {"start": v(6.56, -31.98) * mm, "end": v(7.16, -31.86) * mm});
            skLineSegment(sketch, "E706", {"start": v(7.16, -31.86) * mm, "end": v(7.64, -31.74) * mm});
            skLineSegment(sketch, "E707", {"start": v(7.64, -31.74) * mm, "end": v(8.04, -31.54) * mm});
            skLineSegment(sketch, "E708", {"start": v(8.04, -31.54) * mm, "end": v(8.4, -31.38) * mm});
            skLineSegment(sketch, "E709", {"start": v(8.4, -31.38) * mm, "end": v(8.8, -31.14) * mm});
            skLineSegment(sketch, "E710", {"start": v(8.8, -31.14) * mm, "end": v(9.11, -30.94) * mm});
            skLineSegment(sketch, "E711", {"start": v(9.11, -30.94) * mm, "end": v(9.43, -30.66) * mm});
            skLineSegment(sketch, "E712", {"start": v(9.43, -30.66) * mm, "end": v(9.71, -30.38) * mm});
            skLineSegment(sketch, "E713", {"start": v(9.71, -30.38) * mm, "end": v(10, -30.1) * mm});
            skLineSegment(sketch, "E714", {"start": v(10, -30.1) * mm, "end": v(10.27, -29.78) * mm});
            skLineSegment(sketch, "E715", {"start": v(10.27, -29.78) * mm, "end": v(10.47, -29.46) * mm});
            skLineSegment(sketch, "E716", {"start": v(10.47, -29.46) * mm, "end": v(10.67, -29.1) * mm});
            skLineSegment(sketch, "E717", {"start": v(10.67, -29.1) * mm, "end": v(10.83, -28.74) * mm});
            skLineSegment(sketch, "E718", {"start": v(10.83, -28.74) * mm, "end": v(11, -28.34) * mm});
            skLineSegment(sketch, "E719", {"start": v(11, -28.34) * mm, "end": v(11.07, -27.94) * mm});
            skLineSegment(sketch, "E720", {"start": v(11.07, -27.94) * mm, "end": v(11.15, -27.54) * mm});
            skLineSegment(sketch, "E721", {"start": v(11.15, -27.54) * mm, "end": v(11.2, -27.14) * mm});
            skLineSegment(sketch, "E722", {"start": v(11.2, -27.14) * mm, "end": v(11.23, -26.7) * mm});
            skLineSegment(sketch, "E723", {"start": v(11.23, -26.7) * mm, "end": v(11.2, -26.18) * mm});
            skLineSegment(sketch, "E724", {"start": v(11.2, -26.18) * mm, "end": v(11.11, -25.66) * mm});
            skLineSegment(sketch, "E725", {"start": v(11.11, -25.66) * mm, "end": v(11.03, -25.18) * mm});
            skLineSegment(sketch, "E726", {"start": v(11.03, -25.18) * mm, "end": v(10.87, -24.74) * mm});
            skLineSegment(sketch, "E727", {"start": v(10.87, -24.74) * mm, "end": v(10.67, -24.3) * mm});
            skLineSegment(sketch, "E728", {"start": v(10.67, -24.3) * mm, "end": v(10.47, -23.9) * mm});
            skLineSegment(sketch, "E729", {"start": v(10.47, -23.9) * mm, "end": v(10.2, -23.5) * mm});
            skLineSegment(sketch, "E730", {"start": v(10.2, -23.5) * mm, "end": v(9.87, -23.15) * mm});
            skLineSegment(sketch, "E731", {"start": v(9.87, -23.15) * mm, "end": v(9.51, -22.83) * mm});
            skLineSegment(sketch, "E732", {"start": v(9.51, -22.83) * mm, "end": v(9.15, -22.5) * mm});
            skLineSegment(sketch, "E733", {"start": v(9.15, -22.5) * mm, "end": v(8.75, -22.23) * mm});
            skLineSegment(sketch, "E734", {"start": v(8.75, -22.23) * mm, "end": v(8.35, -21.99) * mm});
            skLineSegment(sketch, "E735", {"start": v(8.35, -21.99) * mm, "end": v(7.92, -21.79) * mm});
            skLineSegment(sketch, "E736", {"start": v(7.92, -21.79) * mm, "end": v(7.48, -21.63) * mm});
            skLineSegment(sketch, "E737", {"start": v(7.48, -21.63) * mm, "end": v(7, -21.5) * mm});
            skLineSegment(sketch, "E738", {"start": v(7, -21.5) * mm, "end": v(6.48, -21.39) * mm});
            skLineSegment(sketch, "E739", {"start": v(6.48, -21.39) * mm, "end": v(6.04, -21.35) * mm});
            skLineSegment(sketch, "E740", {"start": v(6.04, -21.35) * mm, "end": v(5.52, -21.27) * mm});
            skLineSegment(sketch, "E741", {"start": v(5.52, -21.27) * mm, "end": v(4.92, -21.23) * mm});
            skLineSegment(sketch, "E742", {"start": v(4.92, -21.23) * mm, "end": v(4.2, -21.19) * mm});
            skLineSegment(sketch, "E743", {"start": v(4.2, -21.19) * mm, "end": v(3.4, -21.15) * mm});
            skLineSegment(sketch, "E744", {"start": v(3.4, -21.15) * mm, "end": v(2.48, -21.15) * mm});
            skLineSegment(sketch, "E745", {"start": v(2.48, -21.15) * mm, "end": v(1.48, -21.15) * mm});
            skLineSegment(sketch, "E746", {"start": v(1.48, -21.15) * mm, "end": v(0.4, -21.1) * mm});
            skLineSegment(sketch, "E747", {"start": v(0.4, -21.1) * mm, "end": v(-3.68, -21.1) * mm});
            skSolve(sketch);
        }
        {
            var Q0;
            Q0 = qSketchRegion(id + "F0", true);
            var Q1;
            Q1=makeQuery(id+"F0.imprint","IMPRINT",FACE,{"disambiguationData":[TD([[makeQuery(id+"F0.imprint","IMPRINT",EDGE,{"derivedFrom":sQuery(id+"F0.wireOp",EDGE,"E293")}),-1.0]])]});
            var Q2;
            Q2=makeQuery(id+"F0.imprint","IMPRINT",FACE,{"disambiguationData":[TD([[makeQuery(id+"F0.imprint","IMPRINT",EDGE,{"derivedFrom":sQuery(id+"F0.wireOp",EDGE,"E630")}),-1.0]])]});
            var Q3;
            Q3=makeQuery(id+"F0.imprint","IMPRINT",FACE,{"disambiguationData":[TD([[makeQuery(id+"F0.imprint","IMPRINT",EDGE,{"derivedFrom":sQuery(id+"F0.wireOp",EDGE,"E140")}),-1.0]])]});
            extrude(context, id + "F1", {"entities" : qUnion([Q0, Q1, Q2, Q3]), "depth" : 5 * mm});
        }
    });
